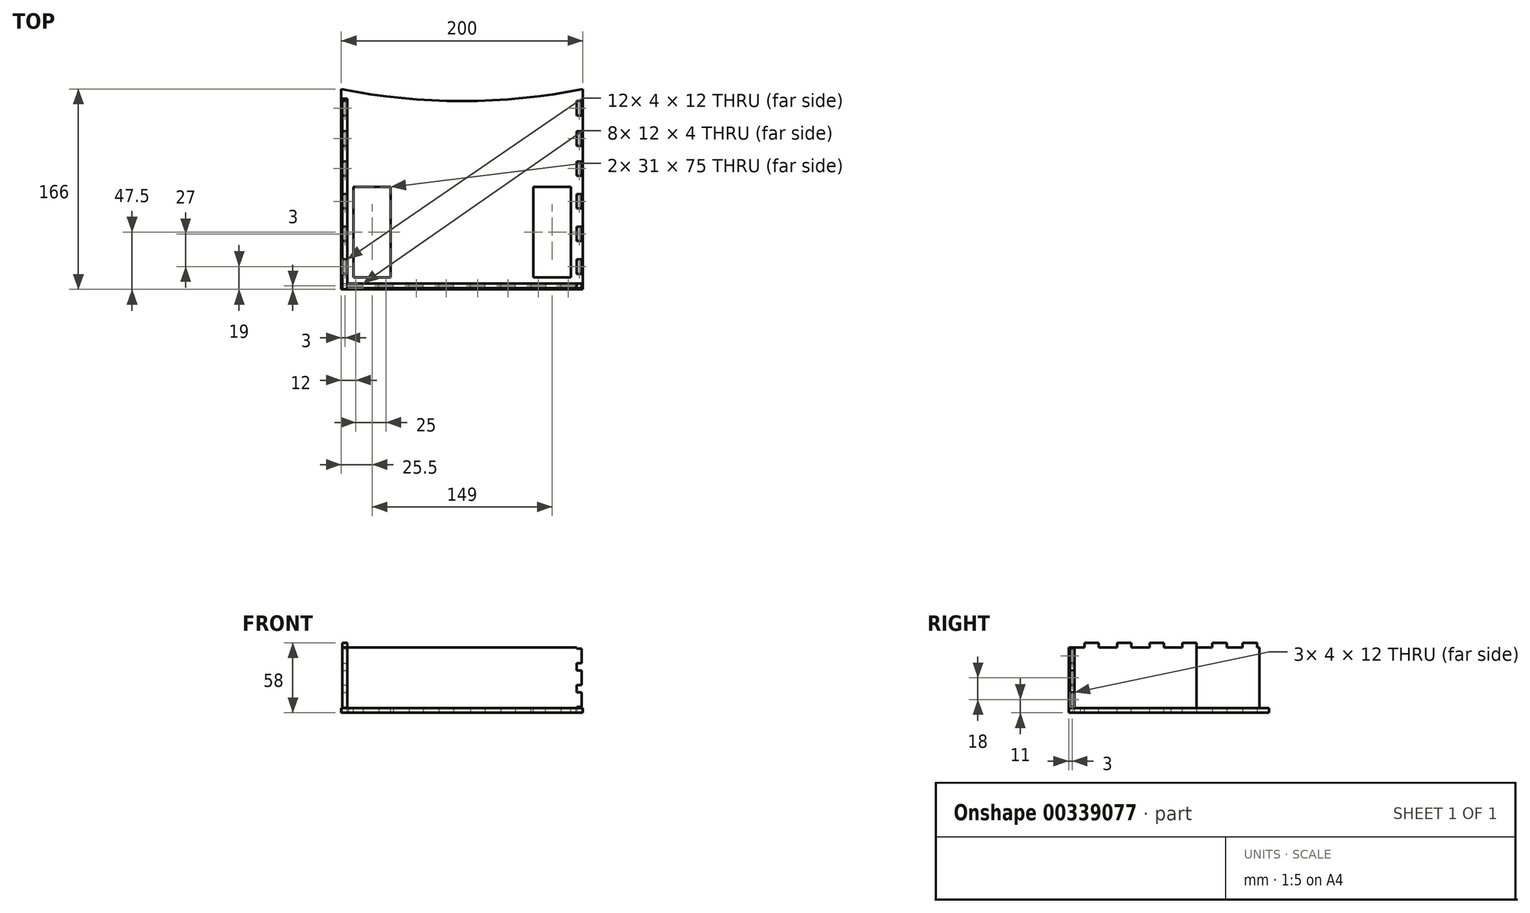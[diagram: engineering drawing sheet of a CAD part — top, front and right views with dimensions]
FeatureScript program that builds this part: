
annotation { "Feature Type Name" : "Feature", "Feature Type Description" : "" }
export const myFeature = defineFeature(function(context is Context, id is Id, definition is map)
    precondition{}
    {
        {
            var Q0;
            Q0=qCreatedBy(makeId("Top.planeOp"),FACE);
            var sketch = newSketch(context, id + "F0", { "sketchPlane" : qUnion([Q0])});
            skLineSegment(sketch, "E0.bottom", {"start": v(100, -100) * mm, "end": v(-100, -100) * mm});
            skLineSegment(sketch, "E0.top", {"start": v(100, 100) * mm, "end": v(-100, 100) * mm});
            skLineSegment(sketch, "E0.left", {"start": v(100, -100) * mm, "end": v(100, 100) * mm});
            skLineSegment(sketch, "E0.right", {"start": v(-100, -100) * mm, "end": v(-100, 100) * mm});
            skPoint(sketch, "E0.middle", {"position": v(0, 0) * mm});
            skLineSegment(sketch, "E1", {"start": v(-140.37, 0) * mm, "end": v(161.21, 0) * mm, "construction": true});
            skLineSegment(sketch, "E2", {"start": v(0, -122.63) * mm, "end": v(0, 131.56) * mm, "construction": true});
            skLineSegment(sketch, "E3.bottom", {"start": v(-95, -6) * mm, "end": v(-99, -6) * mm});
            skLineSegment(sketch, "E3.top", {"start": v(-95, 6) * mm, "end": v(-99, 6) * mm});
            skLineSegment(sketch, "E3.left", {"start": v(-95, -6) * mm, "end": v(-95, 6) * mm});
            skLineSegment(sketch, "E3.right", {"start": v(-99, -6) * mm, "end": v(-99, 6) * mm});
            skPoint(sketch, "E3.middle", {"position": v(-97, 0) * mm});
            skLineSegment(sketch, "E4.0.1.0", {"start": v(-95, -21) * mm, "end": v(-99, -21) * mm});
            skLineSegment(sketch, "E4.0.1.1", {"start": v(-95, -33) * mm, "end": v(-95, -21) * mm});
            skLineSegment(sketch, "E4.0.1.2", {"start": v(-99, -33) * mm, "end": v(-99, -21) * mm});
            skLineSegment(sketch, "E4.0.1.3", {"start": v(-95, -33) * mm, "end": v(-99, -33) * mm});
            skLineSegment(sketch, "E4.0.2.0", {"start": v(-95, -48) * mm, "end": v(-99, -48) * mm});
            skLineSegment(sketch, "E4.0.2.1", {"start": v(-95, -60) * mm, "end": v(-95, -48) * mm});
            skLineSegment(sketch, "E4.0.2.2", {"start": v(-99, -60) * mm, "end": v(-99, -48) * mm});
            skLineSegment(sketch, "E4.0.2.3", {"start": v(-95, -60) * mm, "end": v(-99, -60) * mm});
            skLineSegment(sketch, "E4.0.3.0", {"start": v(-95, -75) * mm, "end": v(-99, -75) * mm});
            skLineSegment(sketch, "E4.0.3.1", {"start": v(-95, -87) * mm, "end": v(-95, -75) * mm});
            skLineSegment(sketch, "E4.0.3.2", {"start": v(-99, -87) * mm, "end": v(-99, -75) * mm});
            skLineSegment(sketch, "E4.0.3.3", {"start": v(-95, -87) * mm, "end": v(-99, -87) * mm});
            skLineSegment(sketch, "E4.direction1", {"start": v(-99, 6) * mm, "end": v(-74, 6) * mm, "construction": true});
            skLineSegment(sketch, "E4.direction2", {"start": v(-99, 6) * mm, "end": v(-99, -21) * mm, "construction": true});
            skLineSegment(sketch, "E5.bottom", {"start": v(-82, -99) * mm, "end": v(-94, -99) * mm});
            skLineSegment(sketch, "E5.top", {"start": v(-82, -95) * mm, "end": v(-94, -95) * mm});
            skLineSegment(sketch, "E5.left", {"start": v(-82, -99) * mm, "end": v(-82, -95) * mm});
            skLineSegment(sketch, "E5.right", {"start": v(-94, -99) * mm, "end": v(-94, -95) * mm});
            skPoint(sketch, "E5.middle", {"position": v(-88, -97) * mm});
            skLineSegment(sketch, "E6.1.0.0", {"start": v(-57, -95) * mm, "end": v(-69, -95) * mm});
            skLineSegment(sketch, "E6.1.0.1", {"start": v(-69, -99) * mm, "end": v(-69, -95) * mm});
            skLineSegment(sketch, "E6.1.0.2", {"start": v(-57, -99) * mm, "end": v(-69, -99) * mm});
            skLineSegment(sketch, "E6.1.0.3", {"start": v(-57, -99) * mm, "end": v(-57, -95) * mm});
            skLineSegment(sketch, "E6.2.0.0", {"start": v(-32, -95) * mm, "end": v(-44, -95) * mm});
            skLineSegment(sketch, "E6.2.0.1", {"start": v(-44, -99) * mm, "end": v(-44, -95) * mm});
            skLineSegment(sketch, "E6.2.0.2", {"start": v(-32, -99) * mm, "end": v(-44, -99) * mm});
            skLineSegment(sketch, "E6.2.0.3", {"start": v(-32, -99) * mm, "end": v(-32, -95) * mm});
            skLineSegment(sketch, "E6.3.0.0", {"start": v(-7, -95) * mm, "end": v(-19, -95) * mm});
            skLineSegment(sketch, "E6.3.0.1", {"start": v(-19, -99) * mm, "end": v(-19, -95) * mm});
            skLineSegment(sketch, "E6.3.0.2", {"start": v(-7, -99) * mm, "end": v(-19, -99) * mm});
            skLineSegment(sketch, "E6.3.0.3", {"start": v(-7, -99) * mm, "end": v(-7, -95) * mm});
            skLineSegment(sketch, "E6.direction1", {"start": v(-94, -95) * mm, "end": v(-69, -95) * mm, "construction": true});
            skLineSegment(sketch, "E7.MirrorCS", {"start": v(95, -6) * mm, "end": v(95, 6) * mm});
            skLineSegment(sketch, "E8.MirrorCS", {"start": v(99, 6) * mm, "end": v(74, 6) * mm, "construction": true});
            skLineSegment(sketch, "E9.MirrorCS", {"start": v(95, 6) * mm, "end": v(99, 6) * mm});
            skLineSegment(sketch, "E10.MirrorCS", {"start": v(99, -6) * mm, "end": v(99, 6) * mm});
            skLineSegment(sketch, "E11.MirrorCS", {"start": v(99, 6) * mm, "end": v(99, -21) * mm, "construction": true});
            skLineSegment(sketch, "E12.MirrorCS", {"start": v(95, -21) * mm, "end": v(99, -21) * mm});
            skLineSegment(sketch, "E13.MirrorCS", {"start": v(99, -33) * mm, "end": v(99, -21) * mm});
            skLineSegment(sketch, "E14.MirrorCS", {"start": v(95, -33) * mm, "end": v(95, -21) * mm});
            skLineSegment(sketch, "E15.MirrorCS", {"start": v(95, -33) * mm, "end": v(99, -33) * mm});
            skLineSegment(sketch, "E16.MirrorCS", {"start": v(95, -48) * mm, "end": v(99, -48) * mm});
            skLineSegment(sketch, "E17.MirrorCS", {"start": v(95, -60) * mm, "end": v(95, -48) * mm});
            skLineSegment(sketch, "E18.MirrorCS", {"start": v(99, -60) * mm, "end": v(99, -48) * mm});
            skLineSegment(sketch, "E19.MirrorCS", {"start": v(95, -60) * mm, "end": v(99, -60) * mm});
            skLineSegment(sketch, "E20.MirrorCS", {"start": v(95, -6) * mm, "end": v(99, -6) * mm});
            skLineSegment(sketch, "E21.MirrorCS", {"start": v(95, -75) * mm, "end": v(99, -75) * mm});
            skLineSegment(sketch, "E22.MirrorCS", {"start": v(95, -87) * mm, "end": v(95, -75) * mm});
            skLineSegment(sketch, "E23.MirrorCS", {"start": v(99, -87) * mm, "end": v(99, -75) * mm});
            skLineSegment(sketch, "E24.MirrorCS", {"start": v(95, -87) * mm, "end": v(99, -87) * mm});
            skLineSegment(sketch, "E25.MirrorCS", {"start": v(94, -95) * mm, "end": v(69, -95) * mm, "construction": true});
            skLineSegment(sketch, "E26.MirrorCS", {"start": v(82, -95) * mm, "end": v(94, -95) * mm});
            skLineSegment(sketch, "E27.MirrorCS", {"start": v(82, -99) * mm, "end": v(94, -99) * mm});
            skLineSegment(sketch, "E28.MirrorCS", {"start": v(94, -99) * mm, "end": v(94, -95) * mm});
            skLineSegment(sketch, "E29.MirrorCS", {"start": v(82, -99) * mm, "end": v(82, -95) * mm});
            skLineSegment(sketch, "E30.MirrorCS", {"start": v(69, -99) * mm, "end": v(69, -95) * mm});
            skLineSegment(sketch, "E31.MirrorCS", {"start": v(57, -95) * mm, "end": v(69, -95) * mm});
            skLineSegment(sketch, "E32.MirrorCS", {"start": v(57, -99) * mm, "end": v(69, -99) * mm});
            skLineSegment(sketch, "E33.MirrorCS", {"start": v(57, -99) * mm, "end": v(57, -95) * mm});
            skLineSegment(sketch, "E34.MirrorCS", {"start": v(32, -95) * mm, "end": v(44, -95) * mm});
            skLineSegment(sketch, "E35.MirrorCS", {"start": v(44, -99) * mm, "end": v(44, -95) * mm});
            skLineSegment(sketch, "E36.MirrorCS", {"start": v(32, -99) * mm, "end": v(44, -99) * mm});
            skLineSegment(sketch, "E37.MirrorCS", {"start": v(32, -99) * mm, "end": v(32, -95) * mm});
            skLineSegment(sketch, "E38.MirrorCS", {"start": v(19, -99) * mm, "end": v(19, -95) * mm});
            skLineSegment(sketch, "E39.MirrorCS", {"start": v(7, -99) * mm, "end": v(19, -99) * mm});
            skLineSegment(sketch, "E40.MirrorCS", {"start": v(7, -95) * mm, "end": v(19, -95) * mm});
            skLineSegment(sketch, "E41.MirrorCS", {"start": v(7, -99) * mm, "end": v(7, -95) * mm});
            skLineSegment(sketch, "E42.0.1.0", {"start": v(-95, 19) * mm, "end": v(-95, 31) * mm});
            skLineSegment(sketch, "E42.0.1.1", {"start": v(-95, 19) * mm, "end": v(-99, 19) * mm});
            skLineSegment(sketch, "E42.0.1.2", {"start": v(-99, 19) * mm, "end": v(-99, 31) * mm});
            skLineSegment(sketch, "E42.0.1.3", {"start": v(-95, 31) * mm, "end": v(-99, 31) * mm});
            skLineSegment(sketch, "E42.0.2.0", {"start": v(-95, 44) * mm, "end": v(-95, 56) * mm});
            skLineSegment(sketch, "E42.0.2.1", {"start": v(-95, 44) * mm, "end": v(-99, 44) * mm});
            skLineSegment(sketch, "E42.0.2.2", {"start": v(-99, 44) * mm, "end": v(-99, 56) * mm});
            skLineSegment(sketch, "E42.0.2.3", {"start": v(-95, 56) * mm, "end": v(-99, 56) * mm});
            skLineSegment(sketch, "E42.direction1", {"start": v(-95, -6) * mm, "end": v(-71.9, -6) * mm, "construction": true});
            skLineSegment(sketch, "E42.direction2", {"start": v(-95, -6) * mm, "end": v(-95, 19) * mm, "construction": true});
            skLineSegment(sketch, "E43.MirrorCS", {"start": v(95, 19) * mm, "end": v(99, 19) * mm});
            skLineSegment(sketch, "E44.MirrorCS", {"start": v(95, 19) * mm, "end": v(95, 31) * mm});
            skLineSegment(sketch, "E45.MirrorCS", {"start": v(99, 19) * mm, "end": v(99, 31) * mm});
            skLineSegment(sketch, "E46.MirrorCS", {"start": v(95, 31) * mm, "end": v(99, 31) * mm});
            skLineSegment(sketch, "E47.MirrorCS", {"start": v(95, 44) * mm, "end": v(99, 44) * mm});
            skLineSegment(sketch, "E48.MirrorCS", {"start": v(95, 44) * mm, "end": v(95, 56) * mm});
            skLineSegment(sketch, "E49.MirrorCS", {"start": v(99, 44) * mm, "end": v(99, 56) * mm});
            skLineSegment(sketch, "E50.MirrorCS", {"start": v(95, 56) * mm, "end": v(99, 56) * mm});
            skArc(sketch, "E51", {"start": v(-100, 66) * mm, "mid": v(0, 55.9) * mm, "end": v(100, 66) * mm});
            skSolve(sketch);
        }
        {
            var Q0;
            {var subQ0=sQuery(id+"F0.wireOp",EDGE,"E0.right");var subQ1=sQuery(id+"F0.wireOp",EDGE,"S1ZzJlAN-Aqjr-jeZ6-mYuY-54TrAklQwlQd");var subQ2=makeQuery(id+"F0.imprint","INTERSECT",VERTEX,{"derivedFrom":[subQ1,subQ0]});Q0=makeQuery(id+"F0.imprint","IMPRINT",FACE,{"disambiguationData":[TD([[makeQuery(id+"F0.imprint","IMPRINT",EDGE,{"disambiguationData":[TD([[subQ2,-1.0]])],"derivedFrom":subQ1}),-1.0]])]});}
            var Q1;
            {var subQ0=sQuery(id+"F0.wireOp",EDGE,"E0.left");var subQ1=sQuery(id+"F0.wireOp",EDGE,"S1ZzJlAN-Aqjr-jeZ6-mYuY-54TrAklQwlQd");var subQ2=makeQuery(id+"F0.imprint","INTERSECT",VERTEX,{"derivedFrom":[subQ1,subQ0]});Q1=makeQuery(id+"F0.imprint","IMPRINT",FACE,{"disambiguationData":[TD([[makeQuery(id+"F0.imprint","IMPRINT",EDGE,{"disambiguationData":[TD([[subQ2,1.0]])],"derivedFrom":subQ1}),-1.0]])]});}
            var Q2;
            Q2=makeQuery(id+"F0.imprint","IMPRINT",FACE,{"disambiguationData":[TD([[makeQuery(id+"F0.imprint","IMPRINT",EDGE,{"derivedFrom":sQuery(id+"F0.wireOp",EDGE,"E3.bottom")}),1.0]])]});
            var Q3;
            {var subQ0=sQuery(id+"F0.wireOp",EDGE,"E0.right");var subQ1=sQuery(id+"F0.wireOp",EDGE,"S1ZzJlAN-Aqjr-jeZ6-mYuY-54TrAklQwlQd");var subQ2=makeQuery(id+"F0.imprint","INTERSECT",VERTEX,{"derivedFrom":[subQ1,subQ0]});Q3=makeQuery(id+"F0.imprint","IMPRINT",FACE,{"disambiguationData":[TD([[makeQuery(id+"F0.imprint","IMPRINT",EDGE,{"disambiguationData":[TD([[subQ2,1.0]])],"derivedFrom":subQ1}),-1.0]])]});}
            var Q4;
            {var subQ0=sQuery(id+"F0.wireOp",EDGE,"E0.left");var subQ1=sQuery(id+"F0.wireOp",EDGE,"S1ZzJlAN-Aqjr-jeZ6-mYuY-54TrAklQwlQd");var subQ2=makeQuery(id+"F0.imprint","INTERSECT",VERTEX,{"derivedFrom":[subQ1,subQ0]});Q4=makeQuery(id+"F0.imprint","IMPRINT",FACE,{"disambiguationData":[TD([[makeQuery(id+"F0.imprint","IMPRINT",EDGE,{"disambiguationData":[TD([[subQ2,-1.0]])],"derivedFrom":subQ1}),-1.0]])]});}
            extrude(context, id + "F1", {"entities" : qUnion([Q0, Q1, Q2, Q3, Q4]), "depth" : 4 * mm, "offsetDistance" : 25 * mm, "symmetric" : true});
        }
        {
            var Q0;
            Q0=makeQuery(id+"F1.opExtrude","CAP_FACE",FACE,{"disambiguationData":[OSD([sQuery(id+"F0.wireOp",EDGE,"S1ZzJlAN-Aqjr-jeZ6-mYuY-54TrAklQwlQd"),sQuery(id+"F0.wireOp",EDGE,"E0.bottom"),sQuery(id+"F0.wireOp",EDGE,"E0.left"),sQuery(id+"F0.wireOp",EDGE,"E0.right"),sQuery(id+"F0.wireOp",EDGE,"E3.bottom"),sQuery(id+"F0.wireOp",EDGE,"E3.top"),sQuery(id+"F0.wireOp",EDGE,"E3.left"),sQuery(id+"F0.wireOp",EDGE,"E3.right"),sQuery(id+"F0.wireOp",EDGE,"E4.0.1.0"),sQuery(id+"F0.wireOp",EDGE,"E4.0.1.1"),sQuery(id+"F0.wireOp",EDGE,"E4.0.1.2"),sQuery(id+"F0.wireOp",EDGE,"E4.0.1.3"),sQuery(id+"F0.wireOp",EDGE,"E4.0.2.0"),sQuery(id+"F0.wireOp",EDGE,"E4.0.2.1"),sQuery(id+"F0.wireOp",EDGE,"E4.0.2.2"),sQuery(id+"F0.wireOp",EDGE,"E4.0.2.3"),sQuery(id+"F0.wireOp",EDGE,"E4.0.3.0"),sQuery(id+"F0.wireOp",EDGE,"E4.0.3.1"),sQuery(id+"F0.wireOp",EDGE,"E4.0.3.2"),sQuery(id+"F0.wireOp",EDGE,"E4.0.3.3"),sQuery(id+"F0.wireOp",EDGE,"E5.bottom"),sQuery(id+"F0.wireOp",EDGE,"E5.top"),sQuery(id+"F0.wireOp",EDGE,"E5.left"),sQuery(id+"F0.wireOp",EDGE,"E5.right"),sQuery(id+"F0.wireOp",EDGE,"E6.1.0.0"),sQuery(id+"F0.wireOp",EDGE,"E6.1.0.1"),sQuery(id+"F0.wireOp",EDGE,"E6.1.0.2"),sQuery(id+"F0.wireOp",EDGE,"E6.1.0.3"),sQuery(id+"F0.wireOp",EDGE,"E6.2.0.0"),sQuery(id+"F0.wireOp",EDGE,"E6.2.0.1"),sQuery(id+"F0.wireOp",EDGE,"E6.2.0.2"),sQuery(id+"F0.wireOp",EDGE,"E6.2.0.3"),sQuery(id+"F0.wireOp",EDGE,"E6.3.0.0"),sQuery(id+"F0.wireOp",EDGE,"E6.3.0.1"),sQuery(id+"F0.wireOp",EDGE,"E6.3.0.2"),sQuery(id+"F0.wireOp",EDGE,"E6.3.0.3"),sQuery(id+"F0.wireOp",EDGE,"E7.MirrorCS"),sQuery(id+"F0.wireOp",EDGE,"E9.MirrorCS"),sQuery(id+"F0.wireOp",EDGE,"E10.MirrorCS"),sQuery(id+"F0.wireOp",EDGE,"E12.MirrorCS"),sQuery(id+"F0.wireOp",EDGE,"E13.MirrorCS"),sQuery(id+"F0.wireOp",EDGE,"E14.MirrorCS"),sQuery(id+"F0.wireOp",EDGE,"E15.MirrorCS"),sQuery(id+"F0.wireOp",EDGE,"E16.MirrorCS"),sQuery(id+"F0.wireOp",EDGE,"E17.MirrorCS"),sQuery(id+"F0.wireOp",EDGE,"E18.MirrorCS"),sQuery(id+"F0.wireOp",EDGE,"E19.MirrorCS"),sQuery(id+"F0.wireOp",EDGE,"E20.MirrorCS"),sQuery(id+"F0.wireOp",EDGE,"E21.MirrorCS"),sQuery(id+"F0.wireOp",EDGE,"E22.MirrorCS"),sQuery(id+"F0.wireOp",EDGE,"E23.MirrorCS"),sQuery(id+"F0.wireOp",EDGE,"E24.MirrorCS"),sQuery(id+"F0.wireOp",EDGE,"E26.MirrorCS"),sQuery(id+"F0.wireOp",EDGE,"E27.MirrorCS"),sQuery(id+"F0.wireOp",EDGE,"E28.MirrorCS"),sQuery(id+"F0.wireOp",EDGE,"E29.MirrorCS"),sQuery(id+"F0.wireOp",EDGE,"E30.MirrorCS"),sQuery(id+"F0.wireOp",EDGE,"E31.MirrorCS"),sQuery(id+"F0.wireOp",EDGE,"E32.MirrorCS"),sQuery(id+"F0.wireOp",EDGE,"E33.MirrorCS"),sQuery(id+"F0.wireOp",EDGE,"E34.MirrorCS"),sQuery(id+"F0.wireOp",EDGE,"E35.MirrorCS"),sQuery(id+"F0.wireOp",EDGE,"E36.MirrorCS"),sQuery(id+"F0.wireOp",EDGE,"E37.MirrorCS"),sQuery(id+"F0.wireOp",EDGE,"E38.MirrorCS"),sQuery(id+"F0.wireOp",EDGE,"E39.MirrorCS"),sQuery(id+"F0.wireOp",EDGE,"E40.MirrorCS"),sQuery(id+"F0.wireOp",EDGE,"E41.MirrorCS")])],"isStart":false});
            var sketch = newSketch(context, id + "F2", { "sketchPlane" : qUnion([Q0])});
            skLineSegment(sketch, "E52.0", {"start": v(-95, 6) * mm, "end": v(-99, 6) * mm});
            skLineSegment(sketch, "E53.0", {"start": v(-95, -6) * mm, "end": v(-95, 6) * mm});
            skLineSegment(sketch, "E54.0", {"start": v(-99, -6) * mm, "end": v(-99, 6) * mm});
            skLineSegment(sketch, "E55.0", {"start": v(-95, -6) * mm, "end": v(-99, -6) * mm});
            skLineSegment(sketch, "E56.0", {"start": v(-95, -21) * mm, "end": v(-99, -21) * mm});
            skLineSegment(sketch, "E57.0", {"start": v(-95, -33) * mm, "end": v(-95, -21) * mm});
            skLineSegment(sketch, "E58.0", {"start": v(-99, -33) * mm, "end": v(-99, -21) * mm});
            skLineSegment(sketch, "E59.0.0", {"start": v(-100, -100) * mm, "end": v(100, -100) * mm});
            skLineSegment(sketch, "E59.0.1", {"start": v(100, -100) * mm, "end": v(100, -100) * mm});
            skLineSegment(sketch, "E59.0.3", {"start": v(-100, 0) * mm, "end": v(-100, -100) * mm});
            skLineSegment(sketch, "E60.0.0", {"start": v(-99, -60) * mm, "end": v(-95, -60) * mm});
            skLineSegment(sketch, "E60.0.1", {"start": v(-95, -60) * mm, "end": v(-95, -48) * mm});
            skLineSegment(sketch, "E60.0.2", {"start": v(-95, -48) * mm, "end": v(-99, -48) * mm});
            skLineSegment(sketch, "E60.0.3", {"start": v(-99, -48) * mm, "end": v(-99, -60) * mm});
            skLineSegment(sketch, "E61.0.0", {"start": v(-99, -87) * mm, "end": v(-95, -87) * mm});
            skLineSegment(sketch, "E61.0.1", {"start": v(-95, -87) * mm, "end": v(-95, -75) * mm});
            skLineSegment(sketch, "E61.0.2", {"start": v(-95, -75) * mm, "end": v(-99, -75) * mm});
            skLineSegment(sketch, "E61.0.3", {"start": v(-99, -75) * mm, "end": v(-99, -87) * mm});
            skLineSegment(sketch, "E62.bottom", {"start": v(-99, 6) * mm, "end": v(-95, 6) * mm});
            skLineSegment(sketch, "E62.top", {"start": v(-99, -100) * mm, "end": v(-95, -100) * mm});
            skLineSegment(sketch, "E62.left", {"start": v(-99, 6) * mm, "end": v(-99, -100) * mm});
            skLineSegment(sketch, "E62.right", {"start": v(-95, 6) * mm, "end": v(-95, -100) * mm});
            skSolve(sketch);
        }
        {
            var Q0;
            {var subQ0=sQuery(id+"F2.wireOp",EDGE,"E55.0");Q0=makeQuery(id+"F2.imprint","IMPRINT",FACE,{"disambiguationData":[TD([[makeQuery(id+"F2.imprint","IMPRINT",EDGE,{"derivedFrom":subQ0}),-1.0]])]});}
            var Q1;
            {var subQ0=sQuery(id+"F2.wireOp",EDGE,"E56.0");Q1=makeQuery(id+"F2.imprint","IMPRINT",FACE,{"disambiguationData":[TD([[makeQuery(id+"F2.imprint","IMPRINT",EDGE,{"derivedFrom":subQ0}),1.0]])]});}
            var Q2;
            {var subQ0=sQuery(id+"F2.wireOp",EDGE,"E60.0.0");Q2=makeQuery(id+"F2.imprint","IMPRINT",FACE,{"disambiguationData":[TD([[makeQuery(id+"F2.imprint","IMPRINT",EDGE,{"derivedFrom":subQ0}),-1.0]])]});}
            var Q3;
            {var subQ0=sQuery(id+"F2.wireOp",EDGE,"E61.0.0");Q3=makeQuery(id+"F2.imprint","IMPRINT",FACE,{"disambiguationData":[TD([[makeQuery(id+"F2.imprint","IMPRINT",EDGE,{"derivedFrom":subQ0}),-1.0]])]});}
            var Q4;
            Q4=makeQuery(id+"F1.opExtrude","CAP_FACE",FACE,{"disambiguationData":[OSD([sQuery(id+"F0.wireOp",EDGE,"S1ZzJlAN-Aqjr-jeZ6-mYuY-54TrAklQwlQd"),sQuery(id+"F0.wireOp",EDGE,"E0.bottom"),sQuery(id+"F0.wireOp",EDGE,"E0.left"),sQuery(id+"F0.wireOp",EDGE,"E0.right"),sQuery(id+"F0.wireOp",EDGE,"E3.bottom"),sQuery(id+"F0.wireOp",EDGE,"E3.top"),sQuery(id+"F0.wireOp",EDGE,"E3.left"),sQuery(id+"F0.wireOp",EDGE,"E3.right"),sQuery(id+"F0.wireOp",EDGE,"E4.0.1.0"),sQuery(id+"F0.wireOp",EDGE,"E4.0.1.1"),sQuery(id+"F0.wireOp",EDGE,"E4.0.1.2"),sQuery(id+"F0.wireOp",EDGE,"E4.0.1.3"),sQuery(id+"F0.wireOp",EDGE,"E4.0.2.0"),sQuery(id+"F0.wireOp",EDGE,"E4.0.2.1"),sQuery(id+"F0.wireOp",EDGE,"E4.0.2.2"),sQuery(id+"F0.wireOp",EDGE,"E4.0.2.3"),sQuery(id+"F0.wireOp",EDGE,"E4.0.3.0"),sQuery(id+"F0.wireOp",EDGE,"E4.0.3.1"),sQuery(id+"F0.wireOp",EDGE,"E4.0.3.2"),sQuery(id+"F0.wireOp",EDGE,"E4.0.3.3"),sQuery(id+"F0.wireOp",EDGE,"E5.bottom"),sQuery(id+"F0.wireOp",EDGE,"E5.top"),sQuery(id+"F0.wireOp",EDGE,"E5.left"),sQuery(id+"F0.wireOp",EDGE,"E5.right"),sQuery(id+"F0.wireOp",EDGE,"E6.1.0.0"),sQuery(id+"F0.wireOp",EDGE,"E6.1.0.1"),sQuery(id+"F0.wireOp",EDGE,"E6.1.0.2"),sQuery(id+"F0.wireOp",EDGE,"E6.1.0.3"),sQuery(id+"F0.wireOp",EDGE,"E6.2.0.0"),sQuery(id+"F0.wireOp",EDGE,"E6.2.0.1"),sQuery(id+"F0.wireOp",EDGE,"E6.2.0.2"),sQuery(id+"F0.wireOp",EDGE,"E6.2.0.3"),sQuery(id+"F0.wireOp",EDGE,"E6.3.0.0"),sQuery(id+"F0.wireOp",EDGE,"E6.3.0.1"),sQuery(id+"F0.wireOp",EDGE,"E6.3.0.2"),sQuery(id+"F0.wireOp",EDGE,"E6.3.0.3"),sQuery(id+"F0.wireOp",EDGE,"E7.MirrorCS"),sQuery(id+"F0.wireOp",EDGE,"E9.MirrorCS"),sQuery(id+"F0.wireOp",EDGE,"E10.MirrorCS"),sQuery(id+"F0.wireOp",EDGE,"E12.MirrorCS"),sQuery(id+"F0.wireOp",EDGE,"E13.MirrorCS"),sQuery(id+"F0.wireOp",EDGE,"E14.MirrorCS"),sQuery(id+"F0.wireOp",EDGE,"E15.MirrorCS"),sQuery(id+"F0.wireOp",EDGE,"E16.MirrorCS"),sQuery(id+"F0.wireOp",EDGE,"E17.MirrorCS"),sQuery(id+"F0.wireOp",EDGE,"E18.MirrorCS"),sQuery(id+"F0.wireOp",EDGE,"E19.MirrorCS"),sQuery(id+"F0.wireOp",EDGE,"E20.MirrorCS"),sQuery(id+"F0.wireOp",EDGE,"E21.MirrorCS"),sQuery(id+"F0.wireOp",EDGE,"E22.MirrorCS"),sQuery(id+"F0.wireOp",EDGE,"E23.MirrorCS"),sQuery(id+"F0.wireOp",EDGE,"E24.MirrorCS"),sQuery(id+"F0.wireOp",EDGE,"E26.MirrorCS"),sQuery(id+"F0.wireOp",EDGE,"E27.MirrorCS"),sQuery(id+"F0.wireOp",EDGE,"E28.MirrorCS"),sQuery(id+"F0.wireOp",EDGE,"E29.MirrorCS"),sQuery(id+"F0.wireOp",EDGE,"E30.MirrorCS"),sQuery(id+"F0.wireOp",EDGE,"E31.MirrorCS"),sQuery(id+"F0.wireOp",EDGE,"E32.MirrorCS"),sQuery(id+"F0.wireOp",EDGE,"E33.MirrorCS"),sQuery(id+"F0.wireOp",EDGE,"E34.MirrorCS"),sQuery(id+"F0.wireOp",EDGE,"E35.MirrorCS"),sQuery(id+"F0.wireOp",EDGE,"E36.MirrorCS"),sQuery(id+"F0.wireOp",EDGE,"E37.MirrorCS"),sQuery(id+"F0.wireOp",EDGE,"E38.MirrorCS"),sQuery(id+"F0.wireOp",EDGE,"E39.MirrorCS"),sQuery(id+"F0.wireOp",EDGE,"E40.MirrorCS"),sQuery(id+"F0.wireOp",EDGE,"E41.MirrorCS")])],"isStart":true});
            extrude(context, id + "F3", {"entities" : qUnion([Q0, Q1, Q2, Q3]), "endBound" : BoundingType.UP_TO_SURFACE, "oppositeDirection" : true, "depth" : 9.4 * mm, "endBoundEntityFace" : qUnion([Q4]), "offsetDistance" : 25 * mm});
        }
        {
            var Q0;
            {var subQ0=sQuery(id+"F2.wireOp",EDGE,"E55.0");Q0=makeQuery(id+"F2.imprint","IMPRINT",FACE,{"disambiguationData":[TD([[makeQuery(id+"F2.imprint","IMPRINT",EDGE,{"derivedFrom":subQ0}),-1.0]])]});}
            var Q1;
            {var subQ0=sQuery(id+"F2.wireOp",EDGE,"E55.0");Q1=makeQuery(id+"F2.imprint","IMPRINT",FACE,{"disambiguationData":[TD([[makeQuery(id+"F2.imprint","IMPRINT",EDGE,{"derivedFrom":subQ0}),1.0]])]});}
            var Q2;
            {var subQ0=sQuery(id+"F2.wireOp",EDGE,"E56.0");Q2=makeQuery(id+"F2.imprint","IMPRINT",FACE,{"disambiguationData":[TD([[makeQuery(id+"F2.imprint","IMPRINT",EDGE,{"derivedFrom":subQ0}),1.0]])]});}
            var Q3;
            {var subQ0=sQuery(id+"F2.wireOp",EDGE,"E60.0.2");Q3=makeQuery(id+"F2.imprint","IMPRINT",FACE,{"disambiguationData":[TD([[makeQuery(id+"F2.imprint","IMPRINT",EDGE,{"derivedFrom":subQ0}),-1.0]])]});}
            var Q4;
            {var subQ0=sQuery(id+"F2.wireOp",EDGE,"E60.0.0");Q4=makeQuery(id+"F2.imprint","IMPRINT",FACE,{"disambiguationData":[TD([[makeQuery(id+"F2.imprint","IMPRINT",EDGE,{"derivedFrom":subQ0}),-1.0]])]});}
            var Q5;
            {var subQ0=sQuery(id+"F2.wireOp",EDGE,"E60.0.0");Q5=makeQuery(id+"F2.imprint","IMPRINT",FACE,{"disambiguationData":[TD([[makeQuery(id+"F2.imprint","IMPRINT",EDGE,{"derivedFrom":subQ0}),1.0]])]});}
            var Q6;
            {var subQ0=sQuery(id+"F2.wireOp",EDGE,"E61.0.0");Q6=makeQuery(id+"F2.imprint","IMPRINT",FACE,{"disambiguationData":[TD([[makeQuery(id+"F2.imprint","IMPRINT",EDGE,{"derivedFrom":subQ0}),-1.0]])]});}
            var Q7;
            {var subQ0=sQuery(id+"F2.wireOp",EDGE,"E61.0.0");Q7=makeQuery(id+"F2.imprint","IMPRINT",FACE,{"disambiguationData":[TD([[makeQuery(id+"F2.imprint","IMPRINT",EDGE,{"derivedFrom":subQ0}),1.0]])]});}
            extrude(context, id + "F4", {"entities" : qUnion([Q0, Q1, Q2, Q3, Q4, Q5, Q6, Q7]), "depth" : 50 * mm, "offsetDistance" : 25 * mm});
        }
        {
            var Q0;
            Q0=makeQuery(id+"F3.opExtrude","SWEPT_BODY",BODY,{"disambiguationData":[OSD([sQuery(id+"F0.wireOp",EDGE,"E4.0.1.3"),sQuery(id+"F2.wireOp",EDGE,"E56.0"),sQuery(id+"F2.wireOp",EDGE,"E62.left"),sQuery(id+"F2.wireOp",EDGE,"E62.right")])]});
            var Q1;
            Q1=makeQuery(id+"F3.opExtrude","SWEPT_BODY",BODY,{"disambiguationData":[OSD([sQuery(id+"F2.wireOp",EDGE,"E60.0.0"),sQuery(id+"F2.wireOp",EDGE,"E60.0.2"),sQuery(id+"F2.wireOp",EDGE,"E62.left"),sQuery(id+"F2.wireOp",EDGE,"E62.right")])]});
            var Q2;
            Q2=makeQuery(id+"F3.opExtrude","SWEPT_BODY",BODY,{"disambiguationData":[OSD([sQuery(id+"F2.wireOp",EDGE,"E61.0.0"),sQuery(id+"F2.wireOp",EDGE,"E61.0.2"),sQuery(id+"F2.wireOp",EDGE,"E62.left"),sQuery(id+"F2.wireOp",EDGE,"E62.right")])]});
            var Q3;
            Q3=makeQuery(id+"F4.opExtrude","SWEPT_BODY",BODY,{"disambiguationData":[OSD([sQuery(id+"F2.wireOp",EDGE,"E62.bottom"),sQuery(id+"F2.wireOp",EDGE,"E62.top"),sQuery(id+"F2.wireOp",EDGE,"E62.left"),sQuery(id+"F2.wireOp",EDGE,"E62.right")])]});
            var Q4;
            Q4=makeQuery(id+"F3.opExtrude","SWEPT_BODY",BODY,{"disambiguationData":[OSD([sQuery(id+"F2.wireOp",EDGE,"E55.0"),sQuery(id+"F2.wireOp",EDGE,"E62.bottom"),sQuery(id+"F2.wireOp",EDGE,"E62.left"),sQuery(id+"F2.wireOp",EDGE,"E62.right")])]});
            booleanBodies(context, id + "F5", {"operationType" : BooleanOperationType.UNION, "tools" : qUnion([Q0, Q1, Q2, Q3, Q4])});
        }
        {
            var Q0;
            Q0=makeQuery(id+"F4.opExtrude","CAP_FACE",FACE,{"disambiguationData":[OSD([sQuery(id+"F2.wireOp",EDGE,"E62.bottom"),sQuery(id+"F2.wireOp",EDGE,"E62.top"),sQuery(id+"F2.wireOp",EDGE,"E62.left"),sQuery(id+"F2.wireOp",EDGE,"E62.right")])],"isStart":false});
            var sketch = newSketch(context, id + "F6", { "sketchPlane" : qUnion([Q0])});
            skPoint(sketch, "E63.0", {"position": v(-95, 0) * mm});
            skLineSegment(sketch, "E64.0.0", {"start": v(-95, 6) * mm, "end": v(-95, -6) * mm});
            skLineSegment(sketch, "E64.0.1", {"start": v(-95, -6) * mm, "end": v(-99, -6) * mm});
            skLineSegment(sketch, "E64.0.2", {"start": v(-99, -6) * mm, "end": v(-99, 6) * mm});
            skLineSegment(sketch, "E64.0.3", {"start": v(-99, 6) * mm, "end": v(-95, 6) * mm});
            skLineSegment(sketch, "E65.0.0", {"start": v(-95, -21) * mm, "end": v(-95, -33) * mm});
            skLineSegment(sketch, "E65.0.1", {"start": v(-95, -33) * mm, "end": v(-99, -33) * mm});
            skLineSegment(sketch, "E65.0.2", {"start": v(-99, -33) * mm, "end": v(-99, -21) * mm});
            skLineSegment(sketch, "E65.0.3", {"start": v(-99, -21) * mm, "end": v(-95, -21) * mm});
            skLineSegment(sketch, "E66.0.0", {"start": v(-99, -60) * mm, "end": v(-99, -48) * mm});
            skLineSegment(sketch, "E66.0.1", {"start": v(-99, -48) * mm, "end": v(-95, -48) * mm});
            skLineSegment(sketch, "E66.0.2", {"start": v(-95, -48) * mm, "end": v(-95, -60) * mm});
            skLineSegment(sketch, "E66.0.3", {"start": v(-95, -60) * mm, "end": v(-99, -60) * mm});
            skLineSegment(sketch, "E67.0.0", {"start": v(-99, -87) * mm, "end": v(-99, -75) * mm});
            skLineSegment(sketch, "E67.0.1", {"start": v(-99, -75) * mm, "end": v(-95, -75) * mm});
            skLineSegment(sketch, "E67.0.2", {"start": v(-95, -75) * mm, "end": v(-95, -87) * mm});
            skLineSegment(sketch, "E67.0.3", {"start": v(-95, -87) * mm, "end": v(-99, -87) * mm});
            skSolve(sketch);
        }
        {
            var Q0;
            Q0=makeQuery(id+"F6.imprint","IMPRINT",FACE,{"disambiguationData":[TD([[makeQuery(id+"F6.imprint","IMPRINT",EDGE,{"derivedFrom":sQuery(id+"F6.wireOp",EDGE,"E64.0.0")}),1.0]])]});
            var Q1;
            Q1=makeQuery(id+"F6.imprint","IMPRINT",FACE,{"disambiguationData":[TD([[makeQuery(id+"F6.imprint","IMPRINT",EDGE,{"derivedFrom":sQuery(id+"F6.wireOp",EDGE,"E65.0.0")}),1.0]])]});
            var Q2;
            Q2=makeQuery(id+"F6.imprint","IMPRINT",FACE,{"disambiguationData":[TD([[makeQuery(id+"F6.imprint","IMPRINT",EDGE,{"derivedFrom":sQuery(id+"F6.wireOp",EDGE,"E66.0.0")}),-1.0]])]});
            var Q3;
            Q3=makeQuery(id+"F6.imprint","IMPRINT",FACE,{"disambiguationData":[TD([[makeQuery(id+"F6.imprint","IMPRINT",EDGE,{"derivedFrom":sQuery(id+"F6.wireOp",EDGE,"E67.0.0")}),-1.0]])]});
            extrude(context, id + "F7", {"entities" : qUnion([Q0, Q1, Q2, Q3]), "operationType" : NewBodyOperationType.ADD, "depth" : 4 * mm, "offsetDistance" : 25 * mm});
        }
        {
            var Q0;
            {var subQ0=sQuery(id+"F2.wireOp",EDGE,"E62.right");Q0=makeQuery(id+"F7.boolean.opBoolean","MERGE",FACE,{"derivedFrom":[makeQuery(id+"F5.opBoolean","MERGE",FACE,{"derivedFrom":[makeQuery(id+"F3.opExtrude","SWEPT_FACE",FACE,{"disambiguationData":[OSD([subQ0]),TDD([makeQuery(id+"F2.imprint","IMPRINT",EDGE,{"disambiguationData":[TD([[makeQuery(id+"F2.imprint","INTERSECT",VERTEX,{"derivedFrom":[sQuery(id+"F2.wireOp",EDGE,"E56.0"),subQ0]}),1.0],[makeQuery(id+"F2.imprint","INTERSECT",VERTEX,{"derivedFrom":[makeQuery(id+"F1.opExtrude","CAP_EDGE",EDGE,{"disambiguationData":[OSD([sQuery(id+"F0.wireOp",EDGE,"E4.0.1.3")])],"isStart":false}),subQ0]}),-1.0]])],"derivedFrom":subQ0})])]}),makeQuery(id+"F3.opExtrude","SWEPT_FACE",FACE,{"disambiguationData":[OSD([subQ0]),TDD([makeQuery(id+"F2.imprint","IMPRINT",EDGE,{"disambiguationData":[TD([[makeQuery(id+"F2.imprint","INTERSECT",VERTEX,{"derivedFrom":[sQuery(id+"F2.wireOp",EDGE,"E61.0.2"),subQ0]}),1.0],[makeQuery(id+"F2.imprint","INTERSECT",VERTEX,{"derivedFrom":[sQuery(id+"F2.wireOp",EDGE,"E61.0.0"),subQ0]}),-1.0]])],"derivedFrom":subQ0})])]}),makeQuery(id+"F3.opExtrude","SWEPT_FACE",FACE,{"disambiguationData":[OSD([subQ0]),TDD([makeQuery(id+"F2.imprint","IMPRINT",EDGE,{"disambiguationData":[TD([[makeQuery(id+"F2.imprint","INTERSECT",VERTEX,{"derivedFrom":[sQuery(id+"F2.wireOp",EDGE,"E60.0.2"),subQ0]}),1.0],[makeQuery(id+"F2.imprint","INTERSECT",VERTEX,{"derivedFrom":[sQuery(id+"F2.wireOp",EDGE,"E60.0.0"),subQ0]}),-1.0]])],"derivedFrom":subQ0})])]}),makeQuery(id+"F3.opExtrude","SWEPT_FACE",FACE,{"disambiguationData":[OSD([subQ0]),TDD([makeQuery(id+"F2.imprint","IMPRINT",EDGE,{"disambiguationData":[TD([[makeQuery(id+"F2.imprint","INTERSECT",VERTEX,{"derivedFrom":[sQuery(id+"F2.wireOp",EDGE,"E55.0"),subQ0]}),-1.0],[makeQuery(id+"F2.imprint","INTERSECT",VERTEX,{"derivedFrom":[sQuery(id+"F2.wireOp",EDGE,"E62.bottom"),subQ0]}),1.0]])],"derivedFrom":subQ0})])]}),makeQuery(id+"F4.opExtrude","SWEPT_FACE",FACE,{"disambiguationData":[OSD([subQ0])]})]}),makeQuery(id+"F7.opExtrude","SWEPT_FACE",FACE,{"disambiguationData":[OSD([sQuery(id+"F6.wireOp",EDGE,"E64.0.0")])]}),makeQuery(id+"F7.opExtrude","SWEPT_FACE",FACE,{"disambiguationData":[OSD([sQuery(id+"F6.wireOp",EDGE,"E65.0.0")])]}),makeQuery(id+"F7.opExtrude","SWEPT_FACE",FACE,{"disambiguationData":[OSD([sQuery(id+"F6.wireOp",EDGE,"E66.0.2")])]}),makeQuery(id+"F7.opExtrude","SWEPT_FACE",FACE,{"disambiguationData":[OSD([sQuery(id+"F6.wireOp",EDGE,"E67.0.2")])]})]});}
            var sketch = newSketch(context, id + "F8", { "sketchPlane" : qUnion([Q0])});
            skLineSegment(sketch, "E68.bottom", {"start": v(-95, 3) * mm, "end": v(-99, 3) * mm});
            skLineSegment(sketch, "E68.top", {"start": v(-95, 15) * mm, "end": v(-99, 15) * mm});
            skLineSegment(sketch, "E68.left", {"start": v(-95, 3) * mm, "end": v(-95, 15) * mm});
            skLineSegment(sketch, "E68.right", {"start": v(-99, 3) * mm, "end": v(-99, 15) * mm});
            skPoint(sketch, "E68.middle", {"position": v(-97, 9) * mm});
            skLineSegment(sketch, "E69.0.1.0", {"start": v(-95, 21) * mm, "end": v(-95, 33) * mm});
            skLineSegment(sketch, "E69.0.1.1", {"start": v(-95, 33) * mm, "end": v(-99, 33) * mm});
            skLineSegment(sketch, "E69.0.1.2", {"start": v(-99, 21) * mm, "end": v(-99, 33) * mm});
            skLineSegment(sketch, "E69.0.1.3", {"start": v(-95, 21) * mm, "end": v(-99, 21) * mm});
            skLineSegment(sketch, "E69.0.2.0", {"start": v(-95, 39) * mm, "end": v(-95, 51) * mm});
            skLineSegment(sketch, "E69.0.2.1", {"start": v(-95, 51) * mm, "end": v(-99, 51) * mm});
            skLineSegment(sketch, "E69.0.2.2", {"start": v(-99, 39) * mm, "end": v(-99, 51) * mm});
            skLineSegment(sketch, "E69.0.2.3", {"start": v(-95, 39) * mm, "end": v(-99, 39) * mm});
            skLineSegment(sketch, "E69.direction1", {"start": v(-95, 3) * mm, "end": v(-70, 3) * mm, "construction": true});
            skLineSegment(sketch, "E69.direction2", {"start": v(-95, 3) * mm, "end": v(-95, 21) * mm, "construction": true});
            skSolve(sketch);
        }
        {
            var Q0;
            Q0=makeQuery(id+"F8.imprint","IMPRINT",FACE,{"disambiguationData":[TD([[makeQuery(id+"F8.imprint","IMPRINT",EDGE,{"derivedFrom":sQuery(id+"F8.wireOp",EDGE,"E69.0.2.0")}),1.0]])]});
            var Q1;
            Q1=makeQuery(id+"F8.imprint","IMPRINT",FACE,{"disambiguationData":[TD([[makeQuery(id+"F8.imprint","IMPRINT",EDGE,{"derivedFrom":sQuery(id+"F8.wireOp",EDGE,"E69.0.1.0")}),1.0]])]});
            var Q2;
            Q2=makeQuery(id+"F8.imprint","IMPRINT",FACE,{"disambiguationData":[TD([[makeQuery(id+"F8.imprint","IMPRINT",EDGE,{"derivedFrom":sQuery(id+"F8.wireOp",EDGE,"E68.bottom")}),-1.0]])]});
            var Q3;
            {var subQ0=sQuery(id+"F2.wireOp",EDGE,"E62.left");Q3=makeQuery(id+"F7.boolean.opBoolean","MERGE",FACE,{"derivedFrom":[makeQuery(id+"F5.opBoolean","MERGE",FACE,{"derivedFrom":[makeQuery(id+"F3.opExtrude","SWEPT_FACE",FACE,{"disambiguationData":[OSD([subQ0]),TDD([makeQuery(id+"F2.imprint","IMPRINT",EDGE,{"disambiguationData":[TD([[makeQuery(id+"F2.imprint","INTERSECT",VERTEX,{"derivedFrom":[sQuery(id+"F2.wireOp",EDGE,"E56.0"),subQ0]}),1.0],[makeQuery(id+"F2.imprint","INTERSECT",VERTEX,{"derivedFrom":[makeQuery(id+"F1.opExtrude","CAP_EDGE",EDGE,{"disambiguationData":[OSD([sQuery(id+"F0.wireOp",EDGE,"E4.0.1.3")])],"isStart":false}),subQ0]}),-1.0]])],"derivedFrom":subQ0})])]}),makeQuery(id+"F3.opExtrude","SWEPT_FACE",FACE,{"disambiguationData":[OSD([subQ0]),TDD([makeQuery(id+"F2.imprint","IMPRINT",EDGE,{"disambiguationData":[TD([[makeQuery(id+"F2.imprint","INTERSECT",VERTEX,{"derivedFrom":[sQuery(id+"F2.wireOp",EDGE,"E55.0"),subQ0]}),-1.0],[makeQuery(id+"F2.imprint","INTERSECT",VERTEX,{"derivedFrom":[sQuery(id+"F2.wireOp",EDGE,"E62.bottom"),subQ0]}),1.0]])],"derivedFrom":subQ0})])]}),makeQuery(id+"F3.opExtrude","SWEPT_FACE",FACE,{"disambiguationData":[OSD([subQ0]),TDD([makeQuery(id+"F2.imprint","IMPRINT",EDGE,{"disambiguationData":[TD([[makeQuery(id+"F2.imprint","INTERSECT",VERTEX,{"derivedFrom":[sQuery(id+"F2.wireOp",EDGE,"E61.0.2"),subQ0]}),1.0],[makeQuery(id+"F2.imprint","INTERSECT",VERTEX,{"derivedFrom":[sQuery(id+"F2.wireOp",EDGE,"E61.0.0"),subQ0]}),-1.0]])],"derivedFrom":subQ0})])]}),makeQuery(id+"F3.opExtrude","SWEPT_FACE",FACE,{"disambiguationData":[OSD([subQ0]),TDD([makeQuery(id+"F2.imprint","IMPRINT",EDGE,{"disambiguationData":[TD([[makeQuery(id+"F2.imprint","INTERSECT",VERTEX,{"derivedFrom":[sQuery(id+"F2.wireOp",EDGE,"E60.0.2"),subQ0]}),1.0],[makeQuery(id+"F2.imprint","INTERSECT",VERTEX,{"derivedFrom":[sQuery(id+"F2.wireOp",EDGE,"E60.0.0"),subQ0]}),-1.0]])],"derivedFrom":subQ0})])]}),makeQuery(id+"F4.opExtrude","SWEPT_FACE",FACE,{"disambiguationData":[OSD([subQ0])]})]}),makeQuery(id+"F7.opExtrude","SWEPT_FACE",FACE,{"disambiguationData":[OSD([sQuery(id+"F6.wireOp",EDGE,"E64.0.2")])]}),makeQuery(id+"F7.opExtrude","SWEPT_FACE",FACE,{"disambiguationData":[OSD([sQuery(id+"F6.wireOp",EDGE,"E65.0.2")])]}),makeQuery(id+"F7.opExtrude","SWEPT_FACE",FACE,{"disambiguationData":[OSD([sQuery(id+"F6.wireOp",EDGE,"E66.0.0")])]}),makeQuery(id+"F7.opExtrude","SWEPT_FACE",FACE,{"disambiguationData":[OSD([sQuery(id+"F6.wireOp",EDGE,"E67.0.0")])]})]});}
            extrude(context, id + "F9", {"entities" : qUnion([Q0, Q1, Q2]), "operationType" : NewBodyOperationType.REMOVE, "endBound" : BoundingType.UP_TO_SURFACE, "oppositeDirection" : true, "depth" : 25 * mm, "endBoundEntityFace" : qUnion([Q3]), "offsetDistance" : 25 * mm});
        }
        {
            var Q0;
            Q0=makeQuery(id+"F1.opExtrude","CAP_FACE",FACE,{"disambiguationData":[OSD([sQuery(id+"F0.wireOp",EDGE,"S1ZzJlAN-Aqjr-jeZ6-mYuY-54TrAklQwlQd"),sQuery(id+"F0.wireOp",EDGE,"E0.bottom"),sQuery(id+"F0.wireOp",EDGE,"E0.left"),sQuery(id+"F0.wireOp",EDGE,"E0.right"),sQuery(id+"F0.wireOp",EDGE,"E3.bottom"),sQuery(id+"F0.wireOp",EDGE,"E3.top"),sQuery(id+"F0.wireOp",EDGE,"E3.left"),sQuery(id+"F0.wireOp",EDGE,"E3.right"),sQuery(id+"F0.wireOp",EDGE,"E4.0.1.0"),sQuery(id+"F0.wireOp",EDGE,"E4.0.1.1"),sQuery(id+"F0.wireOp",EDGE,"E4.0.1.2"),sQuery(id+"F0.wireOp",EDGE,"E4.0.1.3"),sQuery(id+"F0.wireOp",EDGE,"E4.0.2.0"),sQuery(id+"F0.wireOp",EDGE,"E4.0.2.1"),sQuery(id+"F0.wireOp",EDGE,"E4.0.2.2"),sQuery(id+"F0.wireOp",EDGE,"E4.0.2.3"),sQuery(id+"F0.wireOp",EDGE,"E4.0.3.0"),sQuery(id+"F0.wireOp",EDGE,"E4.0.3.1"),sQuery(id+"F0.wireOp",EDGE,"E4.0.3.2"),sQuery(id+"F0.wireOp",EDGE,"E4.0.3.3"),sQuery(id+"F0.wireOp",EDGE,"E5.bottom"),sQuery(id+"F0.wireOp",EDGE,"E5.top"),sQuery(id+"F0.wireOp",EDGE,"E5.left"),sQuery(id+"F0.wireOp",EDGE,"E5.right"),sQuery(id+"F0.wireOp",EDGE,"E6.1.0.0"),sQuery(id+"F0.wireOp",EDGE,"E6.1.0.1"),sQuery(id+"F0.wireOp",EDGE,"E6.1.0.2"),sQuery(id+"F0.wireOp",EDGE,"E6.1.0.3"),sQuery(id+"F0.wireOp",EDGE,"E6.2.0.0"),sQuery(id+"F0.wireOp",EDGE,"E6.2.0.1"),sQuery(id+"F0.wireOp",EDGE,"E6.2.0.2"),sQuery(id+"F0.wireOp",EDGE,"E6.2.0.3"),sQuery(id+"F0.wireOp",EDGE,"E6.3.0.0"),sQuery(id+"F0.wireOp",EDGE,"E6.3.0.1"),sQuery(id+"F0.wireOp",EDGE,"E6.3.0.2"),sQuery(id+"F0.wireOp",EDGE,"E6.3.0.3"),sQuery(id+"F0.wireOp",EDGE,"E7.MirrorCS"),sQuery(id+"F0.wireOp",EDGE,"E9.MirrorCS"),sQuery(id+"F0.wireOp",EDGE,"E10.MirrorCS"),sQuery(id+"F0.wireOp",EDGE,"E12.MirrorCS"),sQuery(id+"F0.wireOp",EDGE,"E13.MirrorCS"),sQuery(id+"F0.wireOp",EDGE,"E14.MirrorCS"),sQuery(id+"F0.wireOp",EDGE,"E15.MirrorCS"),sQuery(id+"F0.wireOp",EDGE,"E16.MirrorCS"),sQuery(id+"F0.wireOp",EDGE,"E17.MirrorCS"),sQuery(id+"F0.wireOp",EDGE,"E18.MirrorCS"),sQuery(id+"F0.wireOp",EDGE,"E19.MirrorCS"),sQuery(id+"F0.wireOp",EDGE,"E20.MirrorCS"),sQuery(id+"F0.wireOp",EDGE,"E21.MirrorCS"),sQuery(id+"F0.wireOp",EDGE,"E22.MirrorCS"),sQuery(id+"F0.wireOp",EDGE,"E23.MirrorCS"),sQuery(id+"F0.wireOp",EDGE,"E24.MirrorCS"),sQuery(id+"F0.wireOp",EDGE,"E26.MirrorCS"),sQuery(id+"F0.wireOp",EDGE,"E27.MirrorCS"),sQuery(id+"F0.wireOp",EDGE,"E28.MirrorCS"),sQuery(id+"F0.wireOp",EDGE,"E29.MirrorCS"),sQuery(id+"F0.wireOp",EDGE,"E30.MirrorCS"),sQuery(id+"F0.wireOp",EDGE,"E31.MirrorCS"),sQuery(id+"F0.wireOp",EDGE,"E32.MirrorCS"),sQuery(id+"F0.wireOp",EDGE,"E33.MirrorCS"),sQuery(id+"F0.wireOp",EDGE,"E34.MirrorCS"),sQuery(id+"F0.wireOp",EDGE,"E35.MirrorCS"),sQuery(id+"F0.wireOp",EDGE,"E36.MirrorCS"),sQuery(id+"F0.wireOp",EDGE,"E37.MirrorCS"),sQuery(id+"F0.wireOp",EDGE,"E38.MirrorCS"),sQuery(id+"F0.wireOp",EDGE,"E39.MirrorCS"),sQuery(id+"F0.wireOp",EDGE,"E40.MirrorCS"),sQuery(id+"F0.wireOp",EDGE,"E41.MirrorCS")])],"isStart":false});
            var sketch = newSketch(context, id + "F10", { "sketchPlane" : qUnion([Q0])});
            skLineSegment(sketch, "E70.bottom", {"start": v(-95, -99) * mm, "end": v(95, -99) * mm});
            skLineSegment(sketch, "E70.top", {"start": v(-95, -95) * mm, "end": v(95, -95) * mm});
            skLineSegment(sketch, "E70.left", {"start": v(-95, -99) * mm, "end": v(-95, -95) * mm});
            skLineSegment(sketch, "E70.right", {"start": v(95, -99) * mm, "end": v(95, -95) * mm});
            skSolve(sketch);
        }
        {
            var Q0;
            {var subQ1=makeQuery(id+"F1.opExtrude","CAP_EDGE",EDGE,{"disambiguationData":[OSD([sQuery(id+"F0.wireOp",EDGE,"E5.left")])],"isStart":false});Q0=makeQuery(id+"F10.imprint","IMPRINT",FACE,{"disambiguationData":[TD([[makeQuery(id+"F10.imprint","IMPRINT",EDGE,{"derivedFrom":subQ1}),1.0]])]});}
            var Q1;
            {var subQ1=makeQuery(id+"F1.opExtrude","CAP_EDGE",EDGE,{"disambiguationData":[OSD([sQuery(id+"F0.wireOp",EDGE,"E6.1.0.1")])],"isStart":false});Q1=makeQuery(id+"F10.imprint","IMPRINT",FACE,{"disambiguationData":[TD([[makeQuery(id+"F10.imprint","IMPRINT",EDGE,{"derivedFrom":subQ1}),-1.0]])]});}
            var Q2;
            {var subQ1=makeQuery(id+"F1.opExtrude","CAP_EDGE",EDGE,{"disambiguationData":[OSD([sQuery(id+"F0.wireOp",EDGE,"E6.2.0.1")])],"isStart":false});Q2=makeQuery(id+"F10.imprint","IMPRINT",FACE,{"disambiguationData":[TD([[makeQuery(id+"F10.imprint","IMPRINT",EDGE,{"derivedFrom":subQ1}),-1.0]])]});}
            var Q3;
            {var subQ1=makeQuery(id+"F1.opExtrude","CAP_EDGE",EDGE,{"disambiguationData":[OSD([sQuery(id+"F0.wireOp",EDGE,"E6.3.0.1")])],"isStart":false});Q3=makeQuery(id+"F10.imprint","IMPRINT",FACE,{"disambiguationData":[TD([[makeQuery(id+"F10.imprint","IMPRINT",EDGE,{"derivedFrom":subQ1}),-1.0]])]});}
            var Q4;
            {var subQ1=makeQuery(id+"F1.opExtrude","CAP_EDGE",EDGE,{"disambiguationData":[OSD([sQuery(id+"F0.wireOp",EDGE,"E38.MirrorCS")])],"isStart":false});Q4=makeQuery(id+"F10.imprint","IMPRINT",FACE,{"disambiguationData":[TD([[makeQuery(id+"F10.imprint","IMPRINT",EDGE,{"derivedFrom":subQ1}),1.0]])]});}
            var Q5;
            {var subQ1=makeQuery(id+"F1.opExtrude","CAP_EDGE",EDGE,{"disambiguationData":[OSD([sQuery(id+"F0.wireOp",EDGE,"E35.MirrorCS")])],"isStart":false});Q5=makeQuery(id+"F10.imprint","IMPRINT",FACE,{"disambiguationData":[TD([[makeQuery(id+"F10.imprint","IMPRINT",EDGE,{"derivedFrom":subQ1}),1.0]])]});}
            var Q6;
            {var subQ1=makeQuery(id+"F1.opExtrude","CAP_EDGE",EDGE,{"disambiguationData":[OSD([sQuery(id+"F0.wireOp",EDGE,"E30.MirrorCS")])],"isStart":false});Q6=makeQuery(id+"F10.imprint","IMPRINT",FACE,{"disambiguationData":[TD([[makeQuery(id+"F10.imprint","IMPRINT",EDGE,{"derivedFrom":subQ1}),1.0]])]});}
            var Q7;
            {var subQ2=makeQuery(id+"F1.opExtrude","CAP_EDGE",EDGE,{"disambiguationData":[OSD([sQuery(id+"F0.wireOp",EDGE,"E28.MirrorCS")])],"isStart":false});Q7=makeQuery(id+"F10.imprint","IMPRINT",FACE,{"disambiguationData":[TD([[makeQuery(id+"F10.imprint","IMPRINT",EDGE,{"derivedFrom":subQ2}),1.0]])]});}
            var Q8;
            Q8=makeQuery(id+"F1.opExtrude","CAP_FACE",FACE,{"disambiguationData":[OSD([sQuery(id+"F0.wireOp",EDGE,"S1ZzJlAN-Aqjr-jeZ6-mYuY-54TrAklQwlQd"),sQuery(id+"F0.wireOp",EDGE,"E0.bottom"),sQuery(id+"F0.wireOp",EDGE,"E0.left"),sQuery(id+"F0.wireOp",EDGE,"E0.right"),sQuery(id+"F0.wireOp",EDGE,"E3.bottom"),sQuery(id+"F0.wireOp",EDGE,"E3.top"),sQuery(id+"F0.wireOp",EDGE,"E3.left"),sQuery(id+"F0.wireOp",EDGE,"E3.right"),sQuery(id+"F0.wireOp",EDGE,"E4.0.1.0"),sQuery(id+"F0.wireOp",EDGE,"E4.0.1.1"),sQuery(id+"F0.wireOp",EDGE,"E4.0.1.2"),sQuery(id+"F0.wireOp",EDGE,"E4.0.1.3"),sQuery(id+"F0.wireOp",EDGE,"E4.0.2.0"),sQuery(id+"F0.wireOp",EDGE,"E4.0.2.1"),sQuery(id+"F0.wireOp",EDGE,"E4.0.2.2"),sQuery(id+"F0.wireOp",EDGE,"E4.0.2.3"),sQuery(id+"F0.wireOp",EDGE,"E4.0.3.0"),sQuery(id+"F0.wireOp",EDGE,"E4.0.3.1"),sQuery(id+"F0.wireOp",EDGE,"E4.0.3.2"),sQuery(id+"F0.wireOp",EDGE,"E4.0.3.3"),sQuery(id+"F0.wireOp",EDGE,"E5.bottom"),sQuery(id+"F0.wireOp",EDGE,"E5.top"),sQuery(id+"F0.wireOp",EDGE,"E5.left"),sQuery(id+"F0.wireOp",EDGE,"E5.right"),sQuery(id+"F0.wireOp",EDGE,"E6.1.0.0"),sQuery(id+"F0.wireOp",EDGE,"E6.1.0.1"),sQuery(id+"F0.wireOp",EDGE,"E6.1.0.2"),sQuery(id+"F0.wireOp",EDGE,"E6.1.0.3"),sQuery(id+"F0.wireOp",EDGE,"E6.2.0.0"),sQuery(id+"F0.wireOp",EDGE,"E6.2.0.1"),sQuery(id+"F0.wireOp",EDGE,"E6.2.0.2"),sQuery(id+"F0.wireOp",EDGE,"E6.2.0.3"),sQuery(id+"F0.wireOp",EDGE,"E6.3.0.0"),sQuery(id+"F0.wireOp",EDGE,"E6.3.0.1"),sQuery(id+"F0.wireOp",EDGE,"E6.3.0.2"),sQuery(id+"F0.wireOp",EDGE,"E6.3.0.3"),sQuery(id+"F0.wireOp",EDGE,"E7.MirrorCS"),sQuery(id+"F0.wireOp",EDGE,"E9.MirrorCS"),sQuery(id+"F0.wireOp",EDGE,"E10.MirrorCS"),sQuery(id+"F0.wireOp",EDGE,"E12.MirrorCS"),sQuery(id+"F0.wireOp",EDGE,"E13.MirrorCS"),sQuery(id+"F0.wireOp",EDGE,"E14.MirrorCS"),sQuery(id+"F0.wireOp",EDGE,"E15.MirrorCS"),sQuery(id+"F0.wireOp",EDGE,"E16.MirrorCS"),sQuery(id+"F0.wireOp",EDGE,"E17.MirrorCS"),sQuery(id+"F0.wireOp",EDGE,"E18.MirrorCS"),sQuery(id+"F0.wireOp",EDGE,"E19.MirrorCS"),sQuery(id+"F0.wireOp",EDGE,"E20.MirrorCS"),sQuery(id+"F0.wireOp",EDGE,"E21.MirrorCS"),sQuery(id+"F0.wireOp",EDGE,"E22.MirrorCS"),sQuery(id+"F0.wireOp",EDGE,"E23.MirrorCS"),sQuery(id+"F0.wireOp",EDGE,"E24.MirrorCS"),sQuery(id+"F0.wireOp",EDGE,"E26.MirrorCS"),sQuery(id+"F0.wireOp",EDGE,"E27.MirrorCS"),sQuery(id+"F0.wireOp",EDGE,"E28.MirrorCS"),sQuery(id+"F0.wireOp",EDGE,"E29.MirrorCS"),sQuery(id+"F0.wireOp",EDGE,"E30.MirrorCS"),sQuery(id+"F0.wireOp",EDGE,"E31.MirrorCS"),sQuery(id+"F0.wireOp",EDGE,"E32.MirrorCS"),sQuery(id+"F0.wireOp",EDGE,"E33.MirrorCS"),sQuery(id+"F0.wireOp",EDGE,"E34.MirrorCS"),sQuery(id+"F0.wireOp",EDGE,"E35.MirrorCS"),sQuery(id+"F0.wireOp",EDGE,"E36.MirrorCS"),sQuery(id+"F0.wireOp",EDGE,"E37.MirrorCS"),sQuery(id+"F0.wireOp",EDGE,"E38.MirrorCS"),sQuery(id+"F0.wireOp",EDGE,"E39.MirrorCS"),sQuery(id+"F0.wireOp",EDGE,"E40.MirrorCS"),sQuery(id+"F0.wireOp",EDGE,"E41.MirrorCS")])],"isStart":true});
            extrude(context, id + "F11", {"entities" : qUnion([Q0, Q1, Q2, Q3, Q4, Q5, Q6, Q7]), "endBound" : BoundingType.UP_TO_SURFACE, "oppositeDirection" : true, "depth" : 25 * mm, "endBoundEntityFace" : qUnion([Q8]), "offsetDistance" : 25 * mm});
        }
        {
            var Q0;
            Q0 = qSketchRegion(id + "F10", true);
            extrude(context, id + "F12", {"entities" : qUnion([Q0]), "depth" : 50 * mm, "offsetDistance" : 25 * mm});
        }
        {
            var Q0;
            Q0=makeQuery(id+"F12.opExtrude","SWEPT_FACE",FACE,{"disambiguationData":[OSD([sQuery(id+"F10.wireOp",EDGE,"E70.left")])]});
            var sketch = newSketch(context, id + "F13", { "sketchPlane" : qUnion([Q0])});
            skLineSegment(sketch, "E71.0", {"start": v(99, 51) * mm, "end": v(99, 39) * mm});
            skLineSegment(sketch, "E72.0", {"start": v(95, 51) * mm, "end": v(95, 39) * mm});
            skLineSegment(sketch, "E73.0", {"start": v(99, 51) * mm, "end": v(95, 51) * mm});
            skLineSegment(sketch, "E74.0", {"start": v(99, 39) * mm, "end": v(95, 39) * mm});
            skLineSegment(sketch, "E75.0", {"start": v(99, 33) * mm, "end": v(95, 33) * mm});
            skLineSegment(sketch, "E76.0", {"start": v(99, 33) * mm, "end": v(99, 21) * mm});
            skLineSegment(sketch, "E77.0", {"start": v(95, 33) * mm, "end": v(95, 21) * mm});
            skLineSegment(sketch, "E78.0", {"start": v(99, 21) * mm, "end": v(95, 21) * mm});
            skLineSegment(sketch, "E79.0", {"start": v(99, 15) * mm, "end": v(95, 15) * mm});
            skLineSegment(sketch, "E80.0", {"start": v(99, 15) * mm, "end": v(99, 3) * mm});
            skLineSegment(sketch, "E81.0", {"start": v(95, 15) * mm, "end": v(95, 3) * mm});
            skLineSegment(sketch, "E82.0", {"start": v(99, 3) * mm, "end": v(95, 3) * mm});
            skSolve(sketch);
        }
        {
            var Q0;
            Q0=makeQuery(id+"F13.imprint","IMPRINT",FACE,{"disambiguationData":[TD([[makeQuery(id+"F13.imprint","IMPRINT",EDGE,{"derivedFrom":sQuery(id+"F13.wireOp",EDGE,"E71.0")}),-1.0]])]});
            var Q1;
            Q1=makeQuery(id+"F13.imprint","IMPRINT",FACE,{"disambiguationData":[TD([[makeQuery(id+"F13.imprint","IMPRINT",EDGE,{"derivedFrom":sQuery(id+"F13.wireOp",EDGE,"E75.0")}),1.0]])]});
            var Q2;
            Q2=makeQuery(id+"F13.imprint","IMPRINT",FACE,{"disambiguationData":[TD([[makeQuery(id+"F13.imprint","IMPRINT",EDGE,{"derivedFrom":sQuery(id+"F13.wireOp",EDGE,"E79.0")}),1.0]])]});
            var Q3;
            {var subQ0=sQuery(id+"F2.wireOp",EDGE,"E62.left");Q3=makeQuery(id+"F7.boolean.opBoolean","MERGE",FACE,{"derivedFrom":[makeQuery(id+"F5.opBoolean","MERGE",FACE,{"derivedFrom":[makeQuery(id+"F3.opExtrude","SWEPT_FACE",FACE,{"disambiguationData":[OSD([subQ0]),TDD([makeQuery(id+"F2.imprint","IMPRINT",EDGE,{"disambiguationData":[TD([[makeQuery(id+"F2.imprint","INTERSECT",VERTEX,{"derivedFrom":[sQuery(id+"F2.wireOp",EDGE,"E56.0"),subQ0]}),1.0],[makeQuery(id+"F2.imprint","INTERSECT",VERTEX,{"derivedFrom":[makeQuery(id+"F1.opExtrude","CAP_EDGE",EDGE,{"disambiguationData":[OSD([sQuery(id+"F0.wireOp",EDGE,"E4.0.1.3")])],"isStart":false}),subQ0]}),-1.0]])],"derivedFrom":subQ0})])]}),makeQuery(id+"F3.opExtrude","SWEPT_FACE",FACE,{"disambiguationData":[OSD([subQ0]),TDD([makeQuery(id+"F2.imprint","IMPRINT",EDGE,{"disambiguationData":[TD([[makeQuery(id+"F2.imprint","INTERSECT",VERTEX,{"derivedFrom":[sQuery(id+"F2.wireOp",EDGE,"E55.0"),subQ0]}),-1.0],[makeQuery(id+"F2.imprint","INTERSECT",VERTEX,{"derivedFrom":[sQuery(id+"F2.wireOp",EDGE,"E62.bottom"),subQ0]}),1.0]])],"derivedFrom":subQ0})])]}),makeQuery(id+"F3.opExtrude","SWEPT_FACE",FACE,{"disambiguationData":[OSD([subQ0]),TDD([makeQuery(id+"F2.imprint","IMPRINT",EDGE,{"disambiguationData":[TD([[makeQuery(id+"F2.imprint","INTERSECT",VERTEX,{"derivedFrom":[sQuery(id+"F2.wireOp",EDGE,"E61.0.2"),subQ0]}),1.0],[makeQuery(id+"F2.imprint","INTERSECT",VERTEX,{"derivedFrom":[sQuery(id+"F2.wireOp",EDGE,"E61.0.0"),subQ0]}),-1.0]])],"derivedFrom":subQ0})])]}),makeQuery(id+"F3.opExtrude","SWEPT_FACE",FACE,{"disambiguationData":[OSD([subQ0]),TDD([makeQuery(id+"F2.imprint","IMPRINT",EDGE,{"disambiguationData":[TD([[makeQuery(id+"F2.imprint","INTERSECT",VERTEX,{"derivedFrom":[sQuery(id+"F2.wireOp",EDGE,"E60.0.2"),subQ0]}),1.0],[makeQuery(id+"F2.imprint","INTERSECT",VERTEX,{"derivedFrom":[sQuery(id+"F2.wireOp",EDGE,"E60.0.0"),subQ0]}),-1.0]])],"derivedFrom":subQ0})])]}),makeQuery(id+"F4.opExtrude","SWEPT_FACE",FACE,{"disambiguationData":[OSD([subQ0])]})]}),makeQuery(id+"F7.opExtrude","SWEPT_FACE",FACE,{"disambiguationData":[OSD([sQuery(id+"F6.wireOp",EDGE,"E64.0.2")])]}),makeQuery(id+"F7.opExtrude","SWEPT_FACE",FACE,{"disambiguationData":[OSD([sQuery(id+"F6.wireOp",EDGE,"E65.0.2")])]}),makeQuery(id+"F7.opExtrude","SWEPT_FACE",FACE,{"disambiguationData":[OSD([sQuery(id+"F6.wireOp",EDGE,"E66.0.0")])]}),makeQuery(id+"F7.opExtrude","SWEPT_FACE",FACE,{"disambiguationData":[OSD([sQuery(id+"F6.wireOp",EDGE,"E67.0.0")])]})]});}
            extrude(context, id + "F14", {"entities" : qUnion([Q0, Q1, Q2]), "depth" : 4 * mm, "endBoundEntityFace" : qUnion([Q3]), "offsetDistance" : 25 * mm});
        }
        {
            var Q0;
            Q0=makeQuery(id+"F12.opExtrude","SWEPT_FACE",FACE,{"disambiguationData":[OSD([sQuery(id+"F10.wireOp",EDGE,"E70.right")])]});
            var sketch = newSketch(context, id + "F15", { "sketchPlane" : qUnion([Q0])});
            skLineSegment(sketch, "E83.0.0", {"start": v(-95, 39) * mm, "end": v(-99, 39) * mm});
            skLineSegment(sketch, "E83.0.1", {"start": v(-99, 39) * mm, "end": v(-99, 51) * mm});
            skLineSegment(sketch, "E83.0.2", {"start": v(-99, 51) * mm, "end": v(-95, 51) * mm});
            skLineSegment(sketch, "E83.0.3", {"start": v(-95, 51) * mm, "end": v(-95, 39) * mm});
            skLineSegment(sketch, "E84.0.0", {"start": v(-95, 21) * mm, "end": v(-99, 21) * mm});
            skLineSegment(sketch, "E84.0.1", {"start": v(-99, 21) * mm, "end": v(-99, 33) * mm});
            skLineSegment(sketch, "E84.0.2", {"start": v(-99, 33) * mm, "end": v(-95, 33) * mm});
            skLineSegment(sketch, "E84.0.3", {"start": v(-95, 33) * mm, "end": v(-95, 21) * mm});
            skLineSegment(sketch, "E85.0.0", {"start": v(-95, 3) * mm, "end": v(-99, 3) * mm});
            skLineSegment(sketch, "E85.0.1", {"start": v(-99, 3) * mm, "end": v(-99, 15) * mm});
            skLineSegment(sketch, "E85.0.2", {"start": v(-99, 15) * mm, "end": v(-95, 15) * mm});
            skLineSegment(sketch, "E85.0.3", {"start": v(-95, 15) * mm, "end": v(-95, 3) * mm});
            skSolve(sketch);
        }
        {
            var Q0;
            Q0=makeQuery(id+"F15.imprint","IMPRINT",FACE,{"disambiguationData":[TD([[makeQuery(id+"F15.imprint","IMPRINT",EDGE,{"derivedFrom":sQuery(id+"F15.wireOp",EDGE,"E83.0.0")}),-1.0]])]});
            var Q1;
            Q1=makeQuery(id+"F15.imprint","IMPRINT",FACE,{"disambiguationData":[TD([[makeQuery(id+"F15.imprint","IMPRINT",EDGE,{"derivedFrom":sQuery(id+"F15.wireOp",EDGE,"E84.0.0")}),-1.0]])]});
            var Q2;
            Q2=makeQuery(id+"F15.imprint","IMPRINT",FACE,{"disambiguationData":[TD([[makeQuery(id+"F15.imprint","IMPRINT",EDGE,{"derivedFrom":sQuery(id+"F15.wireOp",EDGE,"E85.0.0")}),-1.0]])]});
            extrude(context, id + "F16", {"entities" : qUnion([Q0, Q1, Q2]), "operationType" : NewBodyOperationType.ADD, "depth" : 4 * mm, "offsetDistance" : 25 * mm});
        }
        {
            var Q0;
            Q0=makeQuery(id+"F1.opExtrude","CAP_FACE",FACE,{"disambiguationData":[OSD([sQuery(id+"F0.wireOp",EDGE,"S1ZzJlAN-Aqjr-jeZ6-mYuY-54TrAklQwlQd"),sQuery(id+"F0.wireOp",EDGE,"E0.bottom"),sQuery(id+"F0.wireOp",EDGE,"E0.left"),sQuery(id+"F0.wireOp",EDGE,"E0.right"),sQuery(id+"F0.wireOp",EDGE,"E3.bottom"),sQuery(id+"F0.wireOp",EDGE,"E3.top"),sQuery(id+"F0.wireOp",EDGE,"E3.left"),sQuery(id+"F0.wireOp",EDGE,"E3.right"),sQuery(id+"F0.wireOp",EDGE,"E4.0.1.0"),sQuery(id+"F0.wireOp",EDGE,"E4.0.1.1"),sQuery(id+"F0.wireOp",EDGE,"E4.0.1.2"),sQuery(id+"F0.wireOp",EDGE,"E4.0.1.3"),sQuery(id+"F0.wireOp",EDGE,"E4.0.2.0"),sQuery(id+"F0.wireOp",EDGE,"E4.0.2.1"),sQuery(id+"F0.wireOp",EDGE,"E4.0.2.2"),sQuery(id+"F0.wireOp",EDGE,"E4.0.2.3"),sQuery(id+"F0.wireOp",EDGE,"E4.0.3.0"),sQuery(id+"F0.wireOp",EDGE,"E4.0.3.1"),sQuery(id+"F0.wireOp",EDGE,"E4.0.3.2"),sQuery(id+"F0.wireOp",EDGE,"E4.0.3.3"),sQuery(id+"F0.wireOp",EDGE,"E5.bottom"),sQuery(id+"F0.wireOp",EDGE,"E5.top"),sQuery(id+"F0.wireOp",EDGE,"E5.left"),sQuery(id+"F0.wireOp",EDGE,"E5.right"),sQuery(id+"F0.wireOp",EDGE,"E6.1.0.0"),sQuery(id+"F0.wireOp",EDGE,"E6.1.0.1"),sQuery(id+"F0.wireOp",EDGE,"E6.1.0.2"),sQuery(id+"F0.wireOp",EDGE,"E6.1.0.3"),sQuery(id+"F0.wireOp",EDGE,"E6.2.0.0"),sQuery(id+"F0.wireOp",EDGE,"E6.2.0.1"),sQuery(id+"F0.wireOp",EDGE,"E6.2.0.2"),sQuery(id+"F0.wireOp",EDGE,"E6.2.0.3"),sQuery(id+"F0.wireOp",EDGE,"E6.3.0.0"),sQuery(id+"F0.wireOp",EDGE,"E6.3.0.1"),sQuery(id+"F0.wireOp",EDGE,"E6.3.0.2"),sQuery(id+"F0.wireOp",EDGE,"E6.3.0.3"),sQuery(id+"F0.wireOp",EDGE,"E7.MirrorCS"),sQuery(id+"F0.wireOp",EDGE,"E9.MirrorCS"),sQuery(id+"F0.wireOp",EDGE,"E10.MirrorCS"),sQuery(id+"F0.wireOp",EDGE,"E12.MirrorCS"),sQuery(id+"F0.wireOp",EDGE,"E13.MirrorCS"),sQuery(id+"F0.wireOp",EDGE,"E14.MirrorCS"),sQuery(id+"F0.wireOp",EDGE,"E15.MirrorCS"),sQuery(id+"F0.wireOp",EDGE,"E16.MirrorCS"),sQuery(id+"F0.wireOp",EDGE,"E17.MirrorCS"),sQuery(id+"F0.wireOp",EDGE,"E18.MirrorCS"),sQuery(id+"F0.wireOp",EDGE,"E19.MirrorCS"),sQuery(id+"F0.wireOp",EDGE,"E20.MirrorCS"),sQuery(id+"F0.wireOp",EDGE,"E21.MirrorCS"),sQuery(id+"F0.wireOp",EDGE,"E22.MirrorCS"),sQuery(id+"F0.wireOp",EDGE,"E23.MirrorCS"),sQuery(id+"F0.wireOp",EDGE,"E24.MirrorCS"),sQuery(id+"F0.wireOp",EDGE,"E26.MirrorCS"),sQuery(id+"F0.wireOp",EDGE,"E27.MirrorCS"),sQuery(id+"F0.wireOp",EDGE,"E28.MirrorCS"),sQuery(id+"F0.wireOp",EDGE,"E29.MirrorCS"),sQuery(id+"F0.wireOp",EDGE,"E30.MirrorCS"),sQuery(id+"F0.wireOp",EDGE,"E31.MirrorCS"),sQuery(id+"F0.wireOp",EDGE,"E32.MirrorCS"),sQuery(id+"F0.wireOp",EDGE,"E33.MirrorCS"),sQuery(id+"F0.wireOp",EDGE,"E34.MirrorCS"),sQuery(id+"F0.wireOp",EDGE,"E35.MirrorCS"),sQuery(id+"F0.wireOp",EDGE,"E36.MirrorCS"),sQuery(id+"F0.wireOp",EDGE,"E37.MirrorCS"),sQuery(id+"F0.wireOp",EDGE,"E38.MirrorCS"),sQuery(id+"F0.wireOp",EDGE,"E39.MirrorCS"),sQuery(id+"F0.wireOp",EDGE,"E40.MirrorCS"),sQuery(id+"F0.wireOp",EDGE,"E41.MirrorCS")])],"isStart":false});
            var sketch = newSketch(context, id + "F17", { "sketchPlane" : qUnion([Q0])});
            skLineSegment(sketch, "E86.bottom", {"start": v(100, -100) * mm, "end": v(-100, -100) * mm});
            skLineSegment(sketch, "E86.top", {"start": v(100, 100) * mm, "end": v(-100, 100) * mm});
            skLineSegment(sketch, "E86.left", {"start": v(100, -100) * mm, "end": v(100, 100) * mm});
            skLineSegment(sketch, "E86.right", {"start": v(-100, -100) * mm, "end": v(-100, 100) * mm});
            skPoint(sketch, "E86.middle", {"position": v(0, 0) * mm});
            skArc(sketch, "E87", {"start": v(100, 6) * mm, "mid": v(0, 69.33) * mm, "end": v(-100, 6) * mm});
            skSolve(sketch);
        }
        {
            var Q0;
            {var subQ0=sQuery(id+"F17.wireOp",EDGE,"E86.bottom");Q0=makeQuery(id+"F17.imprint","IMPRINT",FACE,{"disambiguationData":[TD([[makeQuery(id+"F17.imprint","IMPRINT",EDGE,{"derivedFrom":subQ0}),-1.0]])]});}
            extrude(context, id + "F18", {"entities" : qUnion([Q0]), "oppositeDirection" : true, "depth" : 4 * mm, "offsetDistance" : 25 * mm});
        }
        {
            var Q0;
            Q0=makeQuery(id+"F1.opExtrude","CAP_FACE",FACE,{"disambiguationData":[OSD([sQuery(id+"F0.wireOp",EDGE,"S1ZzJlAN-Aqjr-jeZ6-mYuY-54TrAklQwlQd"),sQuery(id+"F0.wireOp",EDGE,"E0.bottom"),sQuery(id+"F0.wireOp",EDGE,"E0.left"),sQuery(id+"F0.wireOp",EDGE,"E0.right"),sQuery(id+"F0.wireOp",EDGE,"E3.bottom"),sQuery(id+"F0.wireOp",EDGE,"E3.top"),sQuery(id+"F0.wireOp",EDGE,"E3.left"),sQuery(id+"F0.wireOp",EDGE,"E3.right"),sQuery(id+"F0.wireOp",EDGE,"E4.0.1.0"),sQuery(id+"F0.wireOp",EDGE,"E4.0.1.1"),sQuery(id+"F0.wireOp",EDGE,"E4.0.1.2"),sQuery(id+"F0.wireOp",EDGE,"E4.0.1.3"),sQuery(id+"F0.wireOp",EDGE,"E4.0.2.0"),sQuery(id+"F0.wireOp",EDGE,"E4.0.2.1"),sQuery(id+"F0.wireOp",EDGE,"E4.0.2.2"),sQuery(id+"F0.wireOp",EDGE,"E4.0.2.3"),sQuery(id+"F0.wireOp",EDGE,"E4.0.3.0"),sQuery(id+"F0.wireOp",EDGE,"E4.0.3.1"),sQuery(id+"F0.wireOp",EDGE,"E4.0.3.2"),sQuery(id+"F0.wireOp",EDGE,"E4.0.3.3"),sQuery(id+"F0.wireOp",EDGE,"E5.bottom"),sQuery(id+"F0.wireOp",EDGE,"E5.top"),sQuery(id+"F0.wireOp",EDGE,"E5.left"),sQuery(id+"F0.wireOp",EDGE,"E5.right"),sQuery(id+"F0.wireOp",EDGE,"E6.1.0.0"),sQuery(id+"F0.wireOp",EDGE,"E6.1.0.1"),sQuery(id+"F0.wireOp",EDGE,"E6.1.0.2"),sQuery(id+"F0.wireOp",EDGE,"E6.1.0.3"),sQuery(id+"F0.wireOp",EDGE,"E6.2.0.0"),sQuery(id+"F0.wireOp",EDGE,"E6.2.0.1"),sQuery(id+"F0.wireOp",EDGE,"E6.2.0.2"),sQuery(id+"F0.wireOp",EDGE,"E6.2.0.3"),sQuery(id+"F0.wireOp",EDGE,"E6.3.0.0"),sQuery(id+"F0.wireOp",EDGE,"E6.3.0.1"),sQuery(id+"F0.wireOp",EDGE,"E6.3.0.2"),sQuery(id+"F0.wireOp",EDGE,"E6.3.0.3"),sQuery(id+"F0.wireOp",EDGE,"E7.MirrorCS"),sQuery(id+"F0.wireOp",EDGE,"E9.MirrorCS"),sQuery(id+"F0.wireOp",EDGE,"E10.MirrorCS"),sQuery(id+"F0.wireOp",EDGE,"E12.MirrorCS"),sQuery(id+"F0.wireOp",EDGE,"E13.MirrorCS"),sQuery(id+"F0.wireOp",EDGE,"E14.MirrorCS"),sQuery(id+"F0.wireOp",EDGE,"E15.MirrorCS"),sQuery(id+"F0.wireOp",EDGE,"E16.MirrorCS"),sQuery(id+"F0.wireOp",EDGE,"E17.MirrorCS"),sQuery(id+"F0.wireOp",EDGE,"E18.MirrorCS"),sQuery(id+"F0.wireOp",EDGE,"E19.MirrorCS"),sQuery(id+"F0.wireOp",EDGE,"E20.MirrorCS"),sQuery(id+"F0.wireOp",EDGE,"E21.MirrorCS"),sQuery(id+"F0.wireOp",EDGE,"E22.MirrorCS"),sQuery(id+"F0.wireOp",EDGE,"E23.MirrorCS"),sQuery(id+"F0.wireOp",EDGE,"E24.MirrorCS"),sQuery(id+"F0.wireOp",EDGE,"E26.MirrorCS"),sQuery(id+"F0.wireOp",EDGE,"E27.MirrorCS"),sQuery(id+"F0.wireOp",EDGE,"E28.MirrorCS"),sQuery(id+"F0.wireOp",EDGE,"E29.MirrorCS"),sQuery(id+"F0.wireOp",EDGE,"E30.MirrorCS"),sQuery(id+"F0.wireOp",EDGE,"E31.MirrorCS"),sQuery(id+"F0.wireOp",EDGE,"E32.MirrorCS"),sQuery(id+"F0.wireOp",EDGE,"E33.MirrorCS"),sQuery(id+"F0.wireOp",EDGE,"E34.MirrorCS"),sQuery(id+"F0.wireOp",EDGE,"E35.MirrorCS"),sQuery(id+"F0.wireOp",EDGE,"E36.MirrorCS"),sQuery(id+"F0.wireOp",EDGE,"E37.MirrorCS"),sQuery(id+"F0.wireOp",EDGE,"E38.MirrorCS"),sQuery(id+"F0.wireOp",EDGE,"E39.MirrorCS"),sQuery(id+"F0.wireOp",EDGE,"E40.MirrorCS"),sQuery(id+"F0.wireOp",EDGE,"E41.MirrorCS")])],"isStart":false});
            var sketch = newSketch(context, id + "F19", { "sketchPlane" : qUnion([Q0])});
            skLineSegment(sketch, "E88.bottom", {"start": v(-90, -90) * mm, "end": v(-59, -90) * mm});
            skLineSegment(sketch, "E88.top", {"start": v(-90, -15) * mm, "end": v(-59, -15) * mm});
            skLineSegment(sketch, "E88.left", {"start": v(-90, -90) * mm, "end": v(-90, -15) * mm});
            skLineSegment(sketch, "E88.right", {"start": v(-59, -90) * mm, "end": v(-59, -15) * mm});
            skLineSegment(sketch, "E89", {"start": v(0, 104.15) * mm, "end": v(0, -144.28) * mm, "construction": true});
            skLineSegment(sketch, "E90.MirrorCS", {"start": v(90, -15) * mm, "end": v(59, -15) * mm});
            skLineSegment(sketch, "E91.MirrorCS", {"start": v(59, -90) * mm, "end": v(59, -15) * mm});
            skLineSegment(sketch, "E92.MirrorCS", {"start": v(90, -90) * mm, "end": v(90, -15) * mm});
            skLineSegment(sketch, "E93.MirrorCS", {"start": v(90, -90) * mm, "end": v(59, -90) * mm});
            skSolve(sketch);
        }
        {
            var Q0;
            Q0=makeQuery(id+"F19.imprint","IMPRINT",FACE,{"disambiguationData":[TD([[makeQuery(id+"F19.imprint","IMPRINT",EDGE,{"derivedFrom":sQuery(id+"F19.wireOp",EDGE,"E88.bottom")}),1.0]])]});
            var Q1;
            Q1=makeQuery(id+"F19.imprint","IMPRINT",FACE,{"disambiguationData":[TD([[makeQuery(id+"F19.imprint","IMPRINT",EDGE,{"derivedFrom":sQuery(id+"F19.wireOp",EDGE,"E90.MirrorCS")}),1.0]])]});
            var Q2;
            Q2=makeQuery(id+"F1.opExtrude","CAP_FACE",FACE,{"disambiguationData":[OSD([sQuery(id+"F0.wireOp",EDGE,"S1ZzJlAN-Aqjr-jeZ6-mYuY-54TrAklQwlQd"),sQuery(id+"F0.wireOp",EDGE,"E0.bottom"),sQuery(id+"F0.wireOp",EDGE,"E0.left"),sQuery(id+"F0.wireOp",EDGE,"E0.right"),sQuery(id+"F0.wireOp",EDGE,"E3.bottom"),sQuery(id+"F0.wireOp",EDGE,"E3.top"),sQuery(id+"F0.wireOp",EDGE,"E3.left"),sQuery(id+"F0.wireOp",EDGE,"E3.right"),sQuery(id+"F0.wireOp",EDGE,"E4.0.1.0"),sQuery(id+"F0.wireOp",EDGE,"E4.0.1.1"),sQuery(id+"F0.wireOp",EDGE,"E4.0.1.2"),sQuery(id+"F0.wireOp",EDGE,"E4.0.1.3"),sQuery(id+"F0.wireOp",EDGE,"E4.0.2.0"),sQuery(id+"F0.wireOp",EDGE,"E4.0.2.1"),sQuery(id+"F0.wireOp",EDGE,"E4.0.2.2"),sQuery(id+"F0.wireOp",EDGE,"E4.0.2.3"),sQuery(id+"F0.wireOp",EDGE,"E4.0.3.0"),sQuery(id+"F0.wireOp",EDGE,"E4.0.3.1"),sQuery(id+"F0.wireOp",EDGE,"E4.0.3.2"),sQuery(id+"F0.wireOp",EDGE,"E4.0.3.3"),sQuery(id+"F0.wireOp",EDGE,"E5.bottom"),sQuery(id+"F0.wireOp",EDGE,"E5.top"),sQuery(id+"F0.wireOp",EDGE,"E5.left"),sQuery(id+"F0.wireOp",EDGE,"E5.right"),sQuery(id+"F0.wireOp",EDGE,"E6.1.0.0"),sQuery(id+"F0.wireOp",EDGE,"E6.1.0.1"),sQuery(id+"F0.wireOp",EDGE,"E6.1.0.2"),sQuery(id+"F0.wireOp",EDGE,"E6.1.0.3"),sQuery(id+"F0.wireOp",EDGE,"E6.2.0.0"),sQuery(id+"F0.wireOp",EDGE,"E6.2.0.1"),sQuery(id+"F0.wireOp",EDGE,"E6.2.0.2"),sQuery(id+"F0.wireOp",EDGE,"E6.2.0.3"),sQuery(id+"F0.wireOp",EDGE,"E6.3.0.0"),sQuery(id+"F0.wireOp",EDGE,"E6.3.0.1"),sQuery(id+"F0.wireOp",EDGE,"E6.3.0.2"),sQuery(id+"F0.wireOp",EDGE,"E6.3.0.3"),sQuery(id+"F0.wireOp",EDGE,"E7.MirrorCS"),sQuery(id+"F0.wireOp",EDGE,"E9.MirrorCS"),sQuery(id+"F0.wireOp",EDGE,"E10.MirrorCS"),sQuery(id+"F0.wireOp",EDGE,"E12.MirrorCS"),sQuery(id+"F0.wireOp",EDGE,"E13.MirrorCS"),sQuery(id+"F0.wireOp",EDGE,"E14.MirrorCS"),sQuery(id+"F0.wireOp",EDGE,"E15.MirrorCS"),sQuery(id+"F0.wireOp",EDGE,"E16.MirrorCS"),sQuery(id+"F0.wireOp",EDGE,"E17.MirrorCS"),sQuery(id+"F0.wireOp",EDGE,"E18.MirrorCS"),sQuery(id+"F0.wireOp",EDGE,"E19.MirrorCS"),sQuery(id+"F0.wireOp",EDGE,"E20.MirrorCS"),sQuery(id+"F0.wireOp",EDGE,"E21.MirrorCS"),sQuery(id+"F0.wireOp",EDGE,"E22.MirrorCS"),sQuery(id+"F0.wireOp",EDGE,"E23.MirrorCS"),sQuery(id+"F0.wireOp",EDGE,"E24.MirrorCS"),sQuery(id+"F0.wireOp",EDGE,"E26.MirrorCS"),sQuery(id+"F0.wireOp",EDGE,"E27.MirrorCS"),sQuery(id+"F0.wireOp",EDGE,"E28.MirrorCS"),sQuery(id+"F0.wireOp",EDGE,"E29.MirrorCS"),sQuery(id+"F0.wireOp",EDGE,"E30.MirrorCS"),sQuery(id+"F0.wireOp",EDGE,"E31.MirrorCS"),sQuery(id+"F0.wireOp",EDGE,"E32.MirrorCS"),sQuery(id+"F0.wireOp",EDGE,"E33.MirrorCS"),sQuery(id+"F0.wireOp",EDGE,"E34.MirrorCS"),sQuery(id+"F0.wireOp",EDGE,"E35.MirrorCS"),sQuery(id+"F0.wireOp",EDGE,"E36.MirrorCS"),sQuery(id+"F0.wireOp",EDGE,"E37.MirrorCS"),sQuery(id+"F0.wireOp",EDGE,"E38.MirrorCS"),sQuery(id+"F0.wireOp",EDGE,"E39.MirrorCS"),sQuery(id+"F0.wireOp",EDGE,"E40.MirrorCS"),sQuery(id+"F0.wireOp",EDGE,"E41.MirrorCS")])],"isStart":true});
            extrude(context, id + "F20", {"entities" : qUnion([Q0, Q1]), "operationType" : NewBodyOperationType.REMOVE, "endBound" : BoundingType.UP_TO_SURFACE, "oppositeDirection" : true, "depth" : 25 * mm, "endBoundEntityFace" : qUnion([Q2]), "offsetDistance" : 25 * mm});
        }
        {
            var Q0;
            Q0=makeQuery(id+"F18.opExtrude","SWEPT_BODY",BODY,{"disambiguationData":[OSD([sQuery(id+"F0.wireOp",EDGE,"S1ZzJlAN-Aqjr-jeZ6-mYuY-54TrAklQwlQd"),sQuery(id+"F0.wireOp",EDGE,"E3.bottom"),sQuery(id+"F0.wireOp",EDGE,"E3.top"),sQuery(id+"F0.wireOp",EDGE,"E3.left"),sQuery(id+"F0.wireOp",EDGE,"E3.right"),sQuery(id+"F0.wireOp",EDGE,"E4.0.1.0"),sQuery(id+"F0.wireOp",EDGE,"E4.0.1.1"),sQuery(id+"F0.wireOp",EDGE,"E4.0.1.2"),sQuery(id+"F0.wireOp",EDGE,"E4.0.1.3"),sQuery(id+"F0.wireOp",EDGE,"E4.0.2.0"),sQuery(id+"F0.wireOp",EDGE,"E4.0.2.1"),sQuery(id+"F0.wireOp",EDGE,"E4.0.2.2"),sQuery(id+"F0.wireOp",EDGE,"E4.0.2.3"),sQuery(id+"F0.wireOp",EDGE,"E4.0.3.0"),sQuery(id+"F0.wireOp",EDGE,"E4.0.3.1"),sQuery(id+"F0.wireOp",EDGE,"E4.0.3.2"),sQuery(id+"F0.wireOp",EDGE,"E4.0.3.3"),sQuery(id+"F0.wireOp",EDGE,"E5.bottom"),sQuery(id+"F0.wireOp",EDGE,"E5.top"),sQuery(id+"F0.wireOp",EDGE,"E5.left"),sQuery(id+"F0.wireOp",EDGE,"E5.right"),sQuery(id+"F0.wireOp",EDGE,"E6.1.0.0"),sQuery(id+"F0.wireOp",EDGE,"E6.1.0.1"),sQuery(id+"F0.wireOp",EDGE,"E6.1.0.2"),sQuery(id+"F0.wireOp",EDGE,"E6.1.0.3"),sQuery(id+"F0.wireOp",EDGE,"E6.2.0.0"),sQuery(id+"F0.wireOp",EDGE,"E6.2.0.1"),sQuery(id+"F0.wireOp",EDGE,"E6.2.0.2"),sQuery(id+"F0.wireOp",EDGE,"E6.2.0.3"),sQuery(id+"F0.wireOp",EDGE,"E6.3.0.0"),sQuery(id+"F0.wireOp",EDGE,"E6.3.0.1"),sQuery(id+"F0.wireOp",EDGE,"E6.3.0.2"),sQuery(id+"F0.wireOp",EDGE,"E6.3.0.3"),sQuery(id+"F0.wireOp",EDGE,"E7.MirrorCS"),sQuery(id+"F0.wireOp",EDGE,"E9.MirrorCS"),sQuery(id+"F0.wireOp",EDGE,"E10.MirrorCS"),sQuery(id+"F0.wireOp",EDGE,"E12.MirrorCS"),sQuery(id+"F0.wireOp",EDGE,"E13.MirrorCS"),sQuery(id+"F0.wireOp",EDGE,"E14.MirrorCS"),sQuery(id+"F0.wireOp",EDGE,"E15.MirrorCS"),sQuery(id+"F0.wireOp",EDGE,"E16.MirrorCS"),sQuery(id+"F0.wireOp",EDGE,"E17.MirrorCS"),sQuery(id+"F0.wireOp",EDGE,"E18.MirrorCS"),sQuery(id+"F0.wireOp",EDGE,"E19.MirrorCS"),sQuery(id+"F0.wireOp",EDGE,"E20.MirrorCS"),sQuery(id+"F0.wireOp",EDGE,"E21.MirrorCS"),sQuery(id+"F0.wireOp",EDGE,"E22.MirrorCS"),sQuery(id+"F0.wireOp",EDGE,"E23.MirrorCS"),sQuery(id+"F0.wireOp",EDGE,"E24.MirrorCS"),sQuery(id+"F0.wireOp",EDGE,"E26.MirrorCS"),sQuery(id+"F0.wireOp",EDGE,"E27.MirrorCS"),sQuery(id+"F0.wireOp",EDGE,"E28.MirrorCS"),sQuery(id+"F0.wireOp",EDGE,"E29.MirrorCS"),sQuery(id+"F0.wireOp",EDGE,"E30.MirrorCS"),sQuery(id+"F0.wireOp",EDGE,"E31.MirrorCS"),sQuery(id+"F0.wireOp",EDGE,"E32.MirrorCS"),sQuery(id+"F0.wireOp",EDGE,"E33.MirrorCS"),sQuery(id+"F0.wireOp",EDGE,"E34.MirrorCS"),sQuery(id+"F0.wireOp",EDGE,"E35.MirrorCS"),sQuery(id+"F0.wireOp",EDGE,"E36.MirrorCS"),sQuery(id+"F0.wireOp",EDGE,"E37.MirrorCS"),sQuery(id+"F0.wireOp",EDGE,"E38.MirrorCS"),sQuery(id+"F0.wireOp",EDGE,"E39.MirrorCS"),sQuery(id+"F0.wireOp",EDGE,"E40.MirrorCS"),sQuery(id+"F0.wireOp",EDGE,"E41.MirrorCS"),sQuery(id+"F17.wireOp",EDGE,"E86.bottom"),sQuery(id+"F17.wireOp",EDGE,"E86.left"),sQuery(id+"F17.wireOp",EDGE,"E86.right"),sQuery(id+"F17.wireOp",EDGE,"E87")])]});
            deleteBodies(context, id + "F21", {"entities" : qUnion([Q0])});
        }
        {
            var Q0;
            Q0=makeQuery(id+"F1.opExtrude","CAP_FACE",FACE,{"disambiguationData":[OSD([sQuery(id+"F0.wireOp",EDGE,"E0.bottom"),sQuery(id+"F0.wireOp",EDGE,"E0.left"),sQuery(id+"F0.wireOp",EDGE,"E0.right"),sQuery(id+"F0.wireOp",EDGE,"E3.bottom"),sQuery(id+"F0.wireOp",EDGE,"E3.top"),sQuery(id+"F0.wireOp",EDGE,"E3.left"),sQuery(id+"F0.wireOp",EDGE,"E3.right"),sQuery(id+"F0.wireOp",EDGE,"E4.0.1.0"),sQuery(id+"F0.wireOp",EDGE,"E4.0.1.1"),sQuery(id+"F0.wireOp",EDGE,"E4.0.1.2"),sQuery(id+"F0.wireOp",EDGE,"E4.0.1.3"),sQuery(id+"F0.wireOp",EDGE,"E4.0.2.0"),sQuery(id+"F0.wireOp",EDGE,"E4.0.2.1"),sQuery(id+"F0.wireOp",EDGE,"E4.0.2.2"),sQuery(id+"F0.wireOp",EDGE,"E4.0.2.3"),sQuery(id+"F0.wireOp",EDGE,"E4.0.3.0"),sQuery(id+"F0.wireOp",EDGE,"E4.0.3.1"),sQuery(id+"F0.wireOp",EDGE,"E4.0.3.2"),sQuery(id+"F0.wireOp",EDGE,"E4.0.3.3"),sQuery(id+"F0.wireOp",EDGE,"E5.bottom"),sQuery(id+"F0.wireOp",EDGE,"E5.top"),sQuery(id+"F0.wireOp",EDGE,"E5.left"),sQuery(id+"F0.wireOp",EDGE,"E5.right"),sQuery(id+"F0.wireOp",EDGE,"E6.1.0.0"),sQuery(id+"F0.wireOp",EDGE,"E6.1.0.1"),sQuery(id+"F0.wireOp",EDGE,"E6.1.0.2"),sQuery(id+"F0.wireOp",EDGE,"E6.1.0.3"),sQuery(id+"F0.wireOp",EDGE,"E6.2.0.0"),sQuery(id+"F0.wireOp",EDGE,"E6.2.0.1"),sQuery(id+"F0.wireOp",EDGE,"E6.2.0.2"),sQuery(id+"F0.wireOp",EDGE,"E6.2.0.3"),sQuery(id+"F0.wireOp",EDGE,"E6.3.0.0"),sQuery(id+"F0.wireOp",EDGE,"E6.3.0.1"),sQuery(id+"F0.wireOp",EDGE,"E6.3.0.2"),sQuery(id+"F0.wireOp",EDGE,"E6.3.0.3"),sQuery(id+"F0.wireOp",EDGE,"E7.MirrorCS"),sQuery(id+"F0.wireOp",EDGE,"E9.MirrorCS"),sQuery(id+"F0.wireOp",EDGE,"E10.MirrorCS"),sQuery(id+"F0.wireOp",EDGE,"E12.MirrorCS"),sQuery(id+"F0.wireOp",EDGE,"E13.MirrorCS"),sQuery(id+"F0.wireOp",EDGE,"E14.MirrorCS"),sQuery(id+"F0.wireOp",EDGE,"E15.MirrorCS"),sQuery(id+"F0.wireOp",EDGE,"E16.MirrorCS"),sQuery(id+"F0.wireOp",EDGE,"E17.MirrorCS"),sQuery(id+"F0.wireOp",EDGE,"E18.MirrorCS"),sQuery(id+"F0.wireOp",EDGE,"E19.MirrorCS"),sQuery(id+"F0.wireOp",EDGE,"E20.MirrorCS"),sQuery(id+"F0.wireOp",EDGE,"E21.MirrorCS"),sQuery(id+"F0.wireOp",EDGE,"E22.MirrorCS"),sQuery(id+"F0.wireOp",EDGE,"E23.MirrorCS"),sQuery(id+"F0.wireOp",EDGE,"E24.MirrorCS"),sQuery(id+"F0.wireOp",EDGE,"E26.MirrorCS"),sQuery(id+"F0.wireOp",EDGE,"E27.MirrorCS"),sQuery(id+"F0.wireOp",EDGE,"E28.MirrorCS"),sQuery(id+"F0.wireOp",EDGE,"E29.MirrorCS"),sQuery(id+"F0.wireOp",EDGE,"E30.MirrorCS"),sQuery(id+"F0.wireOp",EDGE,"E31.MirrorCS"),sQuery(id+"F0.wireOp",EDGE,"E32.MirrorCS"),sQuery(id+"F0.wireOp",EDGE,"E33.MirrorCS"),sQuery(id+"F0.wireOp",EDGE,"E34.MirrorCS"),sQuery(id+"F0.wireOp",EDGE,"E35.MirrorCS"),sQuery(id+"F0.wireOp",EDGE,"E36.MirrorCS"),sQuery(id+"F0.wireOp",EDGE,"E37.MirrorCS"),sQuery(id+"F0.wireOp",EDGE,"E38.MirrorCS"),sQuery(id+"F0.wireOp",EDGE,"E39.MirrorCS"),sQuery(id+"F0.wireOp",EDGE,"E40.MirrorCS"),sQuery(id+"F0.wireOp",EDGE,"E41.MirrorCS"),sQuery(id+"F0.wireOp",EDGE,"E42.0.1.0"),sQuery(id+"F0.wireOp",EDGE,"E42.0.1.1"),sQuery(id+"F0.wireOp",EDGE,"E42.0.1.2"),sQuery(id+"F0.wireOp",EDGE,"E42.0.1.3"),sQuery(id+"F0.wireOp",EDGE,"E42.0.2.0"),sQuery(id+"F0.wireOp",EDGE,"E42.0.2.1"),sQuery(id+"F0.wireOp",EDGE,"E42.0.2.2"),sQuery(id+"F0.wireOp",EDGE,"E42.0.2.3"),sQuery(id+"F0.wireOp",EDGE,"E43.MirrorCS"),sQuery(id+"F0.wireOp",EDGE,"E44.MirrorCS"),sQuery(id+"F0.wireOp",EDGE,"E45.MirrorCS"),sQuery(id+"F0.wireOp",EDGE,"E46.MirrorCS"),sQuery(id+"F0.wireOp",EDGE,"E47.MirrorCS"),sQuery(id+"F0.wireOp",EDGE,"E48.MirrorCS"),sQuery(id+"F0.wireOp",EDGE,"E49.MirrorCS"),sQuery(id+"F0.wireOp",EDGE,"E50.MirrorCS"),sQuery(id+"F0.wireOp",EDGE,"E51")])],"isStart":false});
            var sketch = newSketch(context, id + "F22", { "sketchPlane" : qUnion([Q0])});
            skLineSegment(sketch, "E94.bottom", {"start": v(-99, 6) * mm, "end": v(-95, 6) * mm});
            skLineSegment(sketch, "E94.top", {"start": v(-99, 57.97) * mm, "end": v(-95, 57.97) * mm});
            skLineSegment(sketch, "E94.left", {"start": v(-99, 6) * mm, "end": v(-99, 57.97) * mm});
            skLineSegment(sketch, "E94.right", {"start": v(-95, 6) * mm, "end": v(-95, 57.97) * mm});
            skSolve(sketch);
        }
        {
            var Q0;
            {var subQ0=sQuery(id+"F22.wireOp",EDGE,"E94.top");Q0=makeQuery(id+"F22.imprint","IMPRINT",FACE,{"disambiguationData":[TD([[makeQuery(id+"F22.imprint","IMPRINT",EDGE,{"derivedFrom":subQ0}),-1.0]])]});}
            var Q1;
            {var subQ1=makeQuery(id+"F1.opExtrude","CAP_EDGE",EDGE,{"disambiguationData":[OSD([sQuery(id+"F0.wireOp",EDGE,"E42.0.2.1")])],"isStart":false});Q1=makeQuery(id+"F22.imprint","IMPRINT",FACE,{"disambiguationData":[TD([[makeQuery(id+"F22.imprint","IMPRINT",EDGE,{"derivedFrom":subQ1}),-1.0]])]});}
            var Q2;
            {var subQ1=makeQuery(id+"F1.opExtrude","CAP_EDGE",EDGE,{"disambiguationData":[OSD([sQuery(id+"F0.wireOp",EDGE,"E42.0.1.3")])],"isStart":false});Q2=makeQuery(id+"F22.imprint","IMPRINT",FACE,{"disambiguationData":[TD([[makeQuery(id+"F22.imprint","IMPRINT",EDGE,{"derivedFrom":subQ1}),-1.0]])]});}
            var Q3;
            {var subQ1=makeQuery(id+"F1.opExtrude","CAP_EDGE",EDGE,{"disambiguationData":[OSD([sQuery(id+"F0.wireOp",EDGE,"E42.0.1.1")])],"isStart":false});Q3=makeQuery(id+"F22.imprint","IMPRINT",FACE,{"disambiguationData":[TD([[makeQuery(id+"F22.imprint","IMPRINT",EDGE,{"derivedFrom":subQ1}),-1.0]])]});}
            var Q4;
            {var subQ0=sQuery(id+"F22.wireOp",EDGE,"E94.bottom");Q4=makeQuery(id+"F22.imprint","IMPRINT",FACE,{"disambiguationData":[TD([[makeQuery(id+"F22.imprint","IMPRINT",EDGE,{"derivedFrom":subQ0}),-1.0]])]});}
            extrude(context, id + "F23", {"entities" : qUnion([Q0, Q1, Q2, Q3, Q4]), "depth" : 50 * mm, "offsetDistance" : 25 * mm});
        }
        {
            var Q0;
            Q0=makeQuery(id+"F23.opExtrude","CAP_FACE",FACE,{"disambiguationData":[OSD([sQuery(id+"F22.wireOp",EDGE,"E94.bottom"),sQuery(id+"F22.wireOp",EDGE,"E94.top"),sQuery(id+"F22.wireOp",EDGE,"E94.left"),sQuery(id+"F22.wireOp",EDGE,"E94.right")])],"isStart":false});
            var sketch = newSketch(context, id + "F24", { "sketchPlane" : qUnion([Q0])});
            skLineSegment(sketch, "E95.0.0", {"start": v(-95, 19) * mm, "end": v(-95, 31) * mm});
            skLineSegment(sketch, "E95.0.1", {"start": v(-95, 31) * mm, "end": v(-99, 31) * mm});
            skLineSegment(sketch, "E95.0.2", {"start": v(-99, 31) * mm, "end": v(-99, 19) * mm});
            skLineSegment(sketch, "E95.0.3", {"start": v(-99, 19) * mm, "end": v(-95, 19) * mm});
            skLineSegment(sketch, "E96.0.0", {"start": v(-95, 6) * mm, "end": v(-95, -6) * mm});
            skLineSegment(sketch, "E96.0.1", {"start": v(-95, -6) * mm, "end": v(-99, -6) * mm});
            skLineSegment(sketch, "E96.0.2", {"start": v(-99, -6) * mm, "end": v(-99, 6) * mm});
            skLineSegment(sketch, "E96.0.3", {"start": v(-99, 6) * mm, "end": v(-95, 6) * mm});
            skLineSegment(sketch, "E97.0.0", {"start": v(-95, 44) * mm, "end": v(-95, 56) * mm});
            skLineSegment(sketch, "E97.0.1", {"start": v(-95, 56) * mm, "end": v(-99, 56) * mm});
            skLineSegment(sketch, "E97.0.2", {"start": v(-99, 56) * mm, "end": v(-99, 44) * mm});
            skLineSegment(sketch, "E97.0.3", {"start": v(-99, 44) * mm, "end": v(-95, 44) * mm});
            skSolve(sketch);
        }
        {
            var Q0;
            Q0=makeQuery(id+"F24.imprint","IMPRINT",FACE,{"disambiguationData":[TD([[makeQuery(id+"F24.imprint","IMPRINT",EDGE,{"derivedFrom":sQuery(id+"F24.wireOp",EDGE,"E95.0.0")}),1.0]])]});
            var Q1;
            Q1=makeQuery(id+"F24.imprint","IMPRINT",FACE,{"disambiguationData":[TD([[makeQuery(id+"F24.imprint","IMPRINT",EDGE,{"derivedFrom":sQuery(id+"F24.wireOp",EDGE,"E97.0.0")}),1.0]])]});
            extrude(context, id + "F25", {"entities" : qUnion([Q0, Q1]), "operationType" : NewBodyOperationType.ADD, "depth" : 4 * mm, "offsetDistance" : 25 * mm});
        }
        {
            var Q0;
            Q0=makeQuery(id+"F23.opExtrude","CAP_FACE",FACE,{"disambiguationData":[OSD([sQuery(id+"F22.wireOp",EDGE,"E94.bottom"),sQuery(id+"F22.wireOp",EDGE,"E94.top"),sQuery(id+"F22.wireOp",EDGE,"E94.left"),sQuery(id+"F22.wireOp",EDGE,"E94.right")])],"isStart":true});
            var sketch = newSketch(context, id + "F26", { "sketchPlane" : qUnion([Q0])});
            skLineSegment(sketch, "E98.0.0", {"start": v(-95, -44) * mm, "end": v(-95, -56) * mm});
            skLineSegment(sketch, "E98.0.1", {"start": v(-95, -56) * mm, "end": v(-99, -56) * mm});
            skLineSegment(sketch, "E98.0.2", {"start": v(-99, -56) * mm, "end": v(-99, -44) * mm});
            skLineSegment(sketch, "E98.0.3", {"start": v(-99, -44) * mm, "end": v(-95, -44) * mm});
            skLineSegment(sketch, "E99.0.0", {"start": v(-95, -19) * mm, "end": v(-95, -31) * mm});
            skLineSegment(sketch, "E99.0.1", {"start": v(-95, -31) * mm, "end": v(-99, -31) * mm});
            skLineSegment(sketch, "E99.0.2", {"start": v(-99, -31) * mm, "end": v(-99, -19) * mm});
            skLineSegment(sketch, "E99.0.3", {"start": v(-99, -19) * mm, "end": v(-95, -19) * mm});
            skSolve(sketch);
        }
        {
            var Q0;
            Q0=makeQuery(id+"F26.imprint","IMPRINT",FACE,{"disambiguationData":[TD([[makeQuery(id+"F26.imprint","IMPRINT",EDGE,{"derivedFrom":sQuery(id+"F26.wireOp",EDGE,"E98.0.0")}),-1.0]])]});
            var Q1;
            Q1=makeQuery(id+"F26.imprint","IMPRINT",FACE,{"disambiguationData":[TD([[makeQuery(id+"F26.imprint","IMPRINT",EDGE,{"derivedFrom":sQuery(id+"F26.wireOp",EDGE,"E99.0.0")}),-1.0]])]});
            var Q2;
            Q2=makeQuery(id+"F1.opExtrude","CAP_FACE",FACE,{"disambiguationData":[OSD([sQuery(id+"F0.wireOp",EDGE,"E0.bottom"),sQuery(id+"F0.wireOp",EDGE,"E0.left"),sQuery(id+"F0.wireOp",EDGE,"E0.right"),sQuery(id+"F0.wireOp",EDGE,"E3.bottom"),sQuery(id+"F0.wireOp",EDGE,"E3.top"),sQuery(id+"F0.wireOp",EDGE,"E3.left"),sQuery(id+"F0.wireOp",EDGE,"E3.right"),sQuery(id+"F0.wireOp",EDGE,"E4.0.1.0"),sQuery(id+"F0.wireOp",EDGE,"E4.0.1.1"),sQuery(id+"F0.wireOp",EDGE,"E4.0.1.2"),sQuery(id+"F0.wireOp",EDGE,"E4.0.1.3"),sQuery(id+"F0.wireOp",EDGE,"E4.0.2.0"),sQuery(id+"F0.wireOp",EDGE,"E4.0.2.1"),sQuery(id+"F0.wireOp",EDGE,"E4.0.2.2"),sQuery(id+"F0.wireOp",EDGE,"E4.0.2.3"),sQuery(id+"F0.wireOp",EDGE,"E4.0.3.0"),sQuery(id+"F0.wireOp",EDGE,"E4.0.3.1"),sQuery(id+"F0.wireOp",EDGE,"E4.0.3.2"),sQuery(id+"F0.wireOp",EDGE,"E4.0.3.3"),sQuery(id+"F0.wireOp",EDGE,"E5.bottom"),sQuery(id+"F0.wireOp",EDGE,"E5.top"),sQuery(id+"F0.wireOp",EDGE,"E5.left"),sQuery(id+"F0.wireOp",EDGE,"E5.right"),sQuery(id+"F0.wireOp",EDGE,"E6.1.0.0"),sQuery(id+"F0.wireOp",EDGE,"E6.1.0.1"),sQuery(id+"F0.wireOp",EDGE,"E6.1.0.2"),sQuery(id+"F0.wireOp",EDGE,"E6.1.0.3"),sQuery(id+"F0.wireOp",EDGE,"E6.2.0.0"),sQuery(id+"F0.wireOp",EDGE,"E6.2.0.1"),sQuery(id+"F0.wireOp",EDGE,"E6.2.0.2"),sQuery(id+"F0.wireOp",EDGE,"E6.2.0.3"),sQuery(id+"F0.wireOp",EDGE,"E6.3.0.0"),sQuery(id+"F0.wireOp",EDGE,"E6.3.0.1"),sQuery(id+"F0.wireOp",EDGE,"E6.3.0.2"),sQuery(id+"F0.wireOp",EDGE,"E6.3.0.3"),sQuery(id+"F0.wireOp",EDGE,"E7.MirrorCS"),sQuery(id+"F0.wireOp",EDGE,"E9.MirrorCS"),sQuery(id+"F0.wireOp",EDGE,"E10.MirrorCS"),sQuery(id+"F0.wireOp",EDGE,"E12.MirrorCS"),sQuery(id+"F0.wireOp",EDGE,"E13.MirrorCS"),sQuery(id+"F0.wireOp",EDGE,"E14.MirrorCS"),sQuery(id+"F0.wireOp",EDGE,"E15.MirrorCS"),sQuery(id+"F0.wireOp",EDGE,"E16.MirrorCS"),sQuery(id+"F0.wireOp",EDGE,"E17.MirrorCS"),sQuery(id+"F0.wireOp",EDGE,"E18.MirrorCS"),sQuery(id+"F0.wireOp",EDGE,"E19.MirrorCS"),sQuery(id+"F0.wireOp",EDGE,"E20.MirrorCS"),sQuery(id+"F0.wireOp",EDGE,"E21.MirrorCS"),sQuery(id+"F0.wireOp",EDGE,"E22.MirrorCS"),sQuery(id+"F0.wireOp",EDGE,"E23.MirrorCS"),sQuery(id+"F0.wireOp",EDGE,"E24.MirrorCS"),sQuery(id+"F0.wireOp",EDGE,"E26.MirrorCS"),sQuery(id+"F0.wireOp",EDGE,"E27.MirrorCS"),sQuery(id+"F0.wireOp",EDGE,"E28.MirrorCS"),sQuery(id+"F0.wireOp",EDGE,"E29.MirrorCS"),sQuery(id+"F0.wireOp",EDGE,"E30.MirrorCS"),sQuery(id+"F0.wireOp",EDGE,"E31.MirrorCS"),sQuery(id+"F0.wireOp",EDGE,"E32.MirrorCS"),sQuery(id+"F0.wireOp",EDGE,"E33.MirrorCS"),sQuery(id+"F0.wireOp",EDGE,"E34.MirrorCS"),sQuery(id+"F0.wireOp",EDGE,"E35.MirrorCS"),sQuery(id+"F0.wireOp",EDGE,"E36.MirrorCS"),sQuery(id+"F0.wireOp",EDGE,"E37.MirrorCS"),sQuery(id+"F0.wireOp",EDGE,"E38.MirrorCS"),sQuery(id+"F0.wireOp",EDGE,"E39.MirrorCS"),sQuery(id+"F0.wireOp",EDGE,"E40.MirrorCS"),sQuery(id+"F0.wireOp",EDGE,"E41.MirrorCS"),sQuery(id+"F0.wireOp",EDGE,"E42.0.1.0"),sQuery(id+"F0.wireOp",EDGE,"E42.0.1.1"),sQuery(id+"F0.wireOp",EDGE,"E42.0.1.2"),sQuery(id+"F0.wireOp",EDGE,"E42.0.1.3"),sQuery(id+"F0.wireOp",EDGE,"E42.0.2.0"),sQuery(id+"F0.wireOp",EDGE,"E42.0.2.1"),sQuery(id+"F0.wireOp",EDGE,"E42.0.2.2"),sQuery(id+"F0.wireOp",EDGE,"E42.0.2.3"),sQuery(id+"F0.wireOp",EDGE,"E43.MirrorCS"),sQuery(id+"F0.wireOp",EDGE,"E44.MirrorCS"),sQuery(id+"F0.wireOp",EDGE,"E45.MirrorCS"),sQuery(id+"F0.wireOp",EDGE,"E46.MirrorCS"),sQuery(id+"F0.wireOp",EDGE,"E47.MirrorCS"),sQuery(id+"F0.wireOp",EDGE,"E48.MirrorCS"),sQuery(id+"F0.wireOp",EDGE,"E49.MirrorCS"),sQuery(id+"F0.wireOp",EDGE,"E50.MirrorCS"),sQuery(id+"F0.wireOp",EDGE,"E51")])],"isStart":true});
            extrude(context, id + "F27", {"entities" : qUnion([Q0, Q1]), "endBound" : BoundingType.UP_TO_SURFACE, "depth" : 25 * mm, "endBoundEntityFace" : qUnion([Q2]), "offsetDistance" : 25 * mm});
        }
    });
